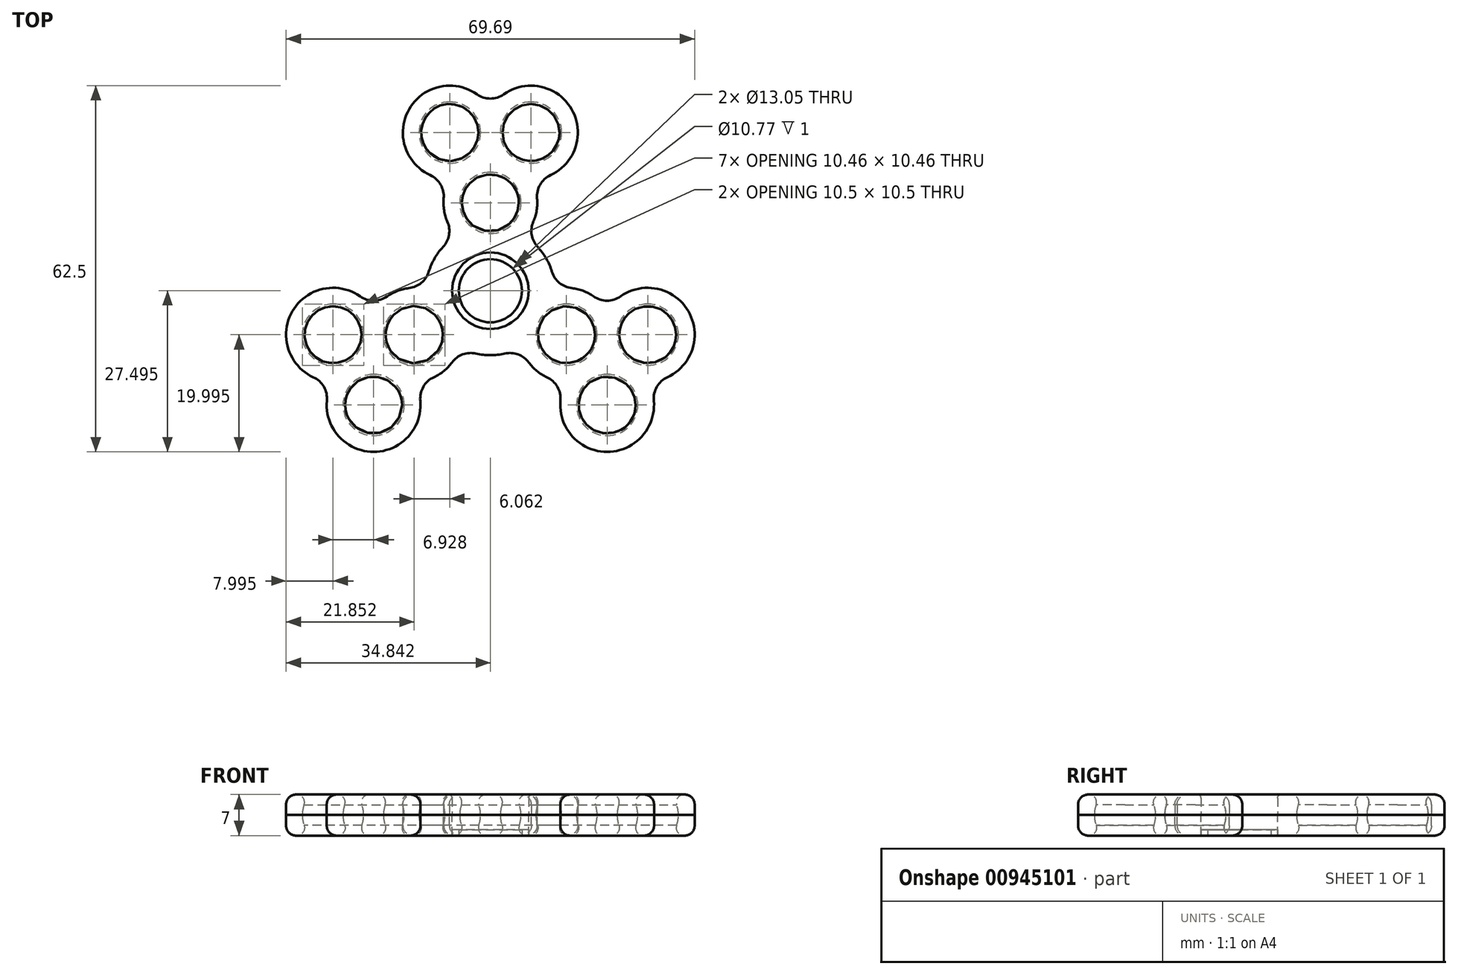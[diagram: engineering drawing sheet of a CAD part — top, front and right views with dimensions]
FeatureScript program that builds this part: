
annotation { "Feature Type Name" : "Feature", "Feature Type Description" : "" }
export const myFeature = defineFeature(function(context is Context, id is Id, definition is map)
    precondition{}
    {
        {
            var Q0;
            Q0=qCreatedBy(makeId("Top.planeOp"),FACE);
            var sketch = newSketch(context, id + "F0", { "sketchPlane" : qUnion([Q0])});
            skCircle(sketch, "E0", {"center": v(73.24, 0.6) * mm, "radius": 6.53 * mm});
            skCircle(sketch, "E1", {"center": v(73.24, 15.6) * mm, "radius": 2.5 * mm});
            skCircle(sketch, "E2", {"center": v(60.25, -6.9) * mm, "radius": 2.5 * mm});
            skCircle(sketch, "E3", {"center": v(86.23, -6.9) * mm, "radius": 2.5 * mm});
            skCircle(sketch, "E4", {"center": v(80.17, 27.6) * mm, "radius": 2.5 * mm});
            skCircle(sketch, "E5", {"center": v(66.31, 27.6) * mm, "radius": 2.5 * mm});
            skCircle(sketch, "E6", {"center": v(46.4, -6.9) * mm, "radius": 2.5 * mm});
            skCircle(sketch, "E7", {"center": v(53.32, -18.9) * mm, "radius": 2.5 * mm});
            skCircle(sketch, "E8", {"center": v(93.16, -18.9) * mm, "radius": 2.5 * mm});
            skCircle(sketch, "E9", {"center": v(100.09, -6.9) * mm, "radius": 2.5 * mm});
            skPoint(sketch, "E10.visualSharp", {"position": v(73.24, 28.6) * mm});
            skPoint(sketch, "E11.visualSharp", {"position": v(68.91, 21.1) * mm});
            skPoint(sketch, "E12.visualSharp", {"position": v(77.57, 21.1) * mm});
            skPoint(sketch, "E13.visualSharp", {"position": v(63.31, -0.6) * mm});
            skPoint(sketch, "E14.visualSharp", {"position": v(67.23, -7.39) * mm});
            skPoint(sketch, "E15.visualSharp", {"position": v(79.25, -7.39) * mm});
            skPoint(sketch, "E16.visualSharp", {"position": v(83.17, -0.6) * mm});
            skPoint(sketch, "E17.visualSharp", {"position": v(77.16, 9.8) * mm});
            skPoint(sketch, "E18.visualSharp", {"position": v(69.32, 9.8) * mm});
            skArc(sketch, "E19.0", {"start": v(59.36, 1.05) * mm, "mid": v(57.4, 0.58) * mm, "end": v(55.63, -0.36) * mm});
            skArc(sketch, "E19.1", {"start": v(65.18, 8.09) * mm, "mid": v(63.72, 6.1) * mm, "end": v(62.73, 3.85) * mm});
            skArc(sketch, "E19.2", {"start": v(65.28, 16.34) * mm, "mid": v(65.34, 14.33) * mm, "end": v(65.9, 12.4) * mm});
            skArc(sketch, "E19.3", {"start": v(70.93, 34.14) * mm, "mid": v(59.39, 31.6) * mm, "end": v(62.97, 20.34) * mm});
            skArc(sketch, "E19.4", {"start": v(79.8, -11.64) * mm, "mid": v(81.18, -13.1) * mm, "end": v(82.88, -14.16) * mm});
            skArc(sketch, "E19.5", {"start": v(70.8, -10.12) * mm, "mid": v(73.24, -10.4) * mm, "end": v(75.69, -10.12) * mm});
            skArc(sketch, "E19.6", {"start": v(63.6, -14.16) * mm, "mid": v(65.3, -13.1) * mm, "end": v(66.69, -11.64) * mm});
            skArc(sketch, "E19.7", {"start": v(45.36, -18.16) * mm, "mid": v(53.32, -26.9) * mm, "end": v(61.29, -18.16) * mm});
            skArc(sketch, "E19.8", {"start": v(85.2, -18.16) * mm, "mid": v(93.16, -26.9) * mm, "end": v(101.13, -18.16) * mm});
            skArc(sketch, "E19.9", {"start": v(103.44, -14.16) * mm, "mid": v(107.02, -2.9) * mm, "end": v(95.47, -0.36) * mm});
            skArc(sketch, "E19.10", {"start": v(90.85, -0.36) * mm, "mid": v(89.08, 0.58) * mm, "end": v(87.13, 1.05) * mm});
            skArc(sketch, "E19.11", {"start": v(83.75, 3.85) * mm, "mid": v(82.77, 6.1) * mm, "end": v(81.3, 8.09) * mm});
            skArc(sketch, "E19.12", {"start": v(51.01, -0.36) * mm, "mid": v(39.47, -2.9) * mm, "end": v(43.05, -14.16) * mm});
            skArc(sketch, "E19.13", {"start": v(80.57, 12.4) * mm, "mid": v(81.14, 14.33) * mm, "end": v(81.2, 16.34) * mm});
            skArc(sketch, "E19.14", {"start": v(83.52, 20.34) * mm, "mid": v(87.1, 31.6) * mm, "end": v(75.55, 34.14) * mm});
            skArc(sketch, "E20.0", {"start": v(45.36, -18.16) * mm, "mid": v(44.84, -15.8) * mm, "end": v(43.05, -14.16) * mm});
            skArc(sketch, "E21.0", {"start": v(63.6, -14.16) * mm, "mid": v(61.8, -15.8) * mm, "end": v(61.29, -18.16) * mm});
            skArc(sketch, "E22.0", {"start": v(70.8, -10.12) * mm, "mid": v(68.52, -10.27) * mm, "end": v(66.69, -11.64) * mm});
            skArc(sketch, "E23.0", {"start": v(79.8, -11.64) * mm, "mid": v(77.97, -10.27) * mm, "end": v(75.69, -10.12) * mm});
            skArc(sketch, "E24.0", {"start": v(85.2, -18.16) * mm, "mid": v(84.68, -15.8) * mm, "end": v(82.88, -14.16) * mm});
            skArc(sketch, "E25.0", {"start": v(103.44, -14.16) * mm, "mid": v(101.65, -15.8) * mm, "end": v(101.13, -18.16) * mm});
            skArc(sketch, "E26.0", {"start": v(90.85, -0.36) * mm, "mid": v(93.16, -1.1) * mm, "end": v(95.47, -0.36) * mm});
            skArc(sketch, "E27.0", {"start": v(83.75, 3.85) * mm, "mid": v(85.02, 1.95) * mm, "end": v(87.13, 1.05) * mm});
            skArc(sketch, "E28.0", {"start": v(80.57, 12.4) * mm, "mid": v(80.3, 10.14) * mm, "end": v(81.3, 8.09) * mm});
            skArc(sketch, "E29.0", {"start": v(83.52, 20.34) * mm, "mid": v(81.73, 18.7) * mm, "end": v(81.2, 16.34) * mm});
            skArc(sketch, "E30.0", {"start": v(65.28, 16.34) * mm, "mid": v(64.76, 18.7) * mm, "end": v(62.97, 20.34) * mm});
            skArc(sketch, "E31.0", {"start": v(65.18, 8.09) * mm, "mid": v(66.19, 10.14) * mm, "end": v(65.9, 12.4) * mm});
            skArc(sketch, "E32.0", {"start": v(59.36, 1.05) * mm, "mid": v(61.46, 1.95) * mm, "end": v(62.73, 3.85) * mm});
            skArc(sketch, "E33.0", {"start": v(51.01, -0.36) * mm, "mid": v(53.32, -1.1) * mm, "end": v(55.63, -0.36) * mm});
            skArc(sketch, "E34.0", {"start": v(70.93, 34.14) * mm, "mid": v(73.24, 33.4) * mm, "end": v(75.55, 34.14) * mm});
            skSolve(sketch);
        }
        {
            var Q0;
            Q0=qSketchRegion(id+"F0",true);
            extrude(context, id + "F1", {"entities" : qUnion([Q0]), "depth" : 3.5 * mm, "offsetDistance" : 25 * mm});
        }
        {
            var Q0;
            Q0=makeQuery(id+"F0.imprint","IMPRINT",FACE,{"disambiguationData":[TD([[makeQuery(id+"F0.imprint","IMPRINT",EDGE,{"derivedFrom":sQuery(id+"F0.wireOp",EDGE,"E0")}),-1.0]])]});
            extrude(context, id + "F2", {"entities" : qUnion([Q0]), "oppositeDirection" : true, "depth" : 3.5 * mm, "offsetDistance" : 25 * mm});
        }
        {
            var Q0;
            Q0=makeQuery(id+"F2.opExtrude","CAP_FACE",FACE,{"disambiguationData":[OSD([sQuery(id+"F0.wireOp",EDGE,"E0"),sQuery(id+"F0.wireOp",EDGE,"tXCEuyxa-6lNA-QPCA-4HXf-ApKYShcEb0Yf"),sQuery(id+"F0.wireOp",EDGE,"E1"),sQuery(id+"F0.wireOp",EDGE,"E2"),sQuery(id+"F0.wireOp",EDGE,"E3"),sQuery(id+"F0.wireOp",EDGE,"E4"),sQuery(id+"F0.wireOp",EDGE,"E5"),sQuery(id+"F0.wireOp",EDGE,"E6"),sQuery(id+"F0.wireOp",EDGE,"E7"),sQuery(id+"F0.wireOp",EDGE,"E8"),sQuery(id+"F0.wireOp",EDGE,"E9"),sQuery(id+"F0.wireOp",EDGE,"0kcF6Lq4-WqBE-dODE-wINV-nyZN5JArXVcS"),sQuery(id+"F0.wireOp",EDGE,"VSrMeVpB-pvXp-ETii-wjF9-Px2PqwZYQnOt"),sQuery(id+"F0.wireOp",EDGE,"OGzEMItw-FQCu-QhKJ-kTiP-AlfaDmg1CYfA"),sQuery(id+"F0.wireOp",EDGE,"E10.filletArc"),sQuery(id+"F0.wireOp",EDGE,"E11.filletArc"),sQuery(id+"F0.wireOp",EDGE,"E12.filletArc"),sQuery(id+"F0.wireOp",EDGE,"61869019-6ff7-477d-8c79-2028de4a396b.trimOffspring"),sQuery(id+"F0.wireOp",EDGE,"b39f1e7b-d492-47c6-a918-6e9c5b166b17"),sQuery(id+"F0.wireOp",EDGE,"9a7d06a7-665d-4e92-ad9d-959fca317462"),sQuery(id+"F0.wireOp",EDGE,"db31c51f-78d2-4091-9bd3-34a254103f45"),sQuery(id+"F0.wireOp",EDGE,"aaf24792-0303-4d5f-86de-c3b2a19fc74e.filletArc"),sQuery(id+"F0.wireOp",EDGE,"5ffe84d5-8cdf-4c2e-9e98-3655a6b86056.filletArc"),sQuery(id+"F0.wireOp",EDGE,"e8945d06-678d-4789-81f5-b1335d2624b7.filletArc"),sQuery(id+"F0.wireOp",EDGE,"a0b45458-2819-4e46-80a9-56e3c7e3f3b4.trimOffspring"),sQuery(id+"F0.wireOp",EDGE,"bf295548-413a-4249-b2ed-de7f7c0a0b82"),sQuery(id+"F0.wireOp",EDGE,"b03dbe81-5cdf-4ba7-a8f7-bb7ec46ab3a8"),sQuery(id+"F0.wireOp",EDGE,"b0d05724-446d-4885-847a-915c569f1139"),sQuery(id+"F0.wireOp",EDGE,"608d76ae-a745-4fd0-ae95-f5732494cd55.filletArc"),sQuery(id+"F0.wireOp",EDGE,"a41367dd-7dbd-4f08-888b-74168a8e5936.filletArc"),sQuery(id+"F0.wireOp",EDGE,"84e31002-7089-4eef-81a0-79c8965d61ed.filletArc"),sQuery(id+"F0.wireOp",EDGE,"1335fa2d-2410-4889-a90b-ae026db059b2.trimOffspring"),sQuery(id+"F0.wireOp",EDGE,"81157b49-ae94-446f-8b4e-5ce1e116e724.trimOffspring"),sQuery(id+"F0.wireOp",EDGE,"4f1c551e-3bfd-48a9-873a-6291d27f8455.trimOffspring"),sQuery(id+"F0.wireOp",EDGE,"E13.filletArc"),sQuery(id+"F0.wireOp",EDGE,"E14.filletArc"),sQuery(id+"F0.wireOp",EDGE,"E15.filletArc"),sQuery(id+"F0.wireOp",EDGE,"E16.filletArc"),sQuery(id+"F0.wireOp",EDGE,"E17.filletArc"),sQuery(id+"F0.wireOp",EDGE,"E18.filletArc")])],"isStart":true});
            var sketch = newSketch(context, id + "F3", { "sketchPlane" : qUnion([Q0])});
            skLineSegment(sketch, "E35", {"start": v(53.32, -18.9) * mm, "end": v(53.32, -24.12) * mm});
            skLineSegment(sketch, "E36", {"start": v(53.32, -18.9) * mm, "end": v(53.32, -13.66) * mm});
            skArc(sketch, "E37", {"start": v(53.32, -13.66) * mm, "mid": v(48.1, -18.9) * mm, "end": v(53.32, -24.12) * mm});
            skSolve(sketch);
        }
        {
            var Q0;
            Q0=qSketchRegion(id+"F3",true);
            var Q1;
            Q1=sQuery(id+"F3.wireOp",EDGE,"E36");
            revolve(context, id + "F4", {"surfaceOperationType" : NewSurfaceOperationType.NEW, "entities" : qUnion([Q0]), "axis" : qUnion([Q1]), "revolveType" : RevolveType.FULL});
        }
        {
            var Q0;
            Q0=makeQuery(id+"F2.opExtrude","CAP_FACE",FACE,{"disambiguationData":[OSD([sQuery(id+"F0.wireOp",EDGE,"E0"),sQuery(id+"F0.wireOp",EDGE,"tXCEuyxa-6lNA-QPCA-4HXf-ApKYShcEb0Yf"),sQuery(id+"F0.wireOp",EDGE,"E1"),sQuery(id+"F0.wireOp",EDGE,"E2"),sQuery(id+"F0.wireOp",EDGE,"E3"),sQuery(id+"F0.wireOp",EDGE,"E4"),sQuery(id+"F0.wireOp",EDGE,"E5"),sQuery(id+"F0.wireOp",EDGE,"E6"),sQuery(id+"F0.wireOp",EDGE,"E7"),sQuery(id+"F0.wireOp",EDGE,"E8"),sQuery(id+"F0.wireOp",EDGE,"E9"),sQuery(id+"F0.wireOp",EDGE,"0kcF6Lq4-WqBE-dODE-wINV-nyZN5JArXVcS"),sQuery(id+"F0.wireOp",EDGE,"VSrMeVpB-pvXp-ETii-wjF9-Px2PqwZYQnOt"),sQuery(id+"F0.wireOp",EDGE,"OGzEMItw-FQCu-QhKJ-kTiP-AlfaDmg1CYfA"),sQuery(id+"F0.wireOp",EDGE,"E10.filletArc"),sQuery(id+"F0.wireOp",EDGE,"E11.filletArc"),sQuery(id+"F0.wireOp",EDGE,"E12.filletArc"),sQuery(id+"F0.wireOp",EDGE,"61869019-6ff7-477d-8c79-2028de4a396b.trimOffspring"),sQuery(id+"F0.wireOp",EDGE,"b39f1e7b-d492-47c6-a918-6e9c5b166b17"),sQuery(id+"F0.wireOp",EDGE,"9a7d06a7-665d-4e92-ad9d-959fca317462"),sQuery(id+"F0.wireOp",EDGE,"db31c51f-78d2-4091-9bd3-34a254103f45"),sQuery(id+"F0.wireOp",EDGE,"aaf24792-0303-4d5f-86de-c3b2a19fc74e.filletArc"),sQuery(id+"F0.wireOp",EDGE,"5ffe84d5-8cdf-4c2e-9e98-3655a6b86056.filletArc"),sQuery(id+"F0.wireOp",EDGE,"e8945d06-678d-4789-81f5-b1335d2624b7.filletArc"),sQuery(id+"F0.wireOp",EDGE,"a0b45458-2819-4e46-80a9-56e3c7e3f3b4.trimOffspring"),sQuery(id+"F0.wireOp",EDGE,"bf295548-413a-4249-b2ed-de7f7c0a0b82"),sQuery(id+"F0.wireOp",EDGE,"b03dbe81-5cdf-4ba7-a8f7-bb7ec46ab3a8"),sQuery(id+"F0.wireOp",EDGE,"b0d05724-446d-4885-847a-915c569f1139"),sQuery(id+"F0.wireOp",EDGE,"608d76ae-a745-4fd0-ae95-f5732494cd55.filletArc"),sQuery(id+"F0.wireOp",EDGE,"a41367dd-7dbd-4f08-888b-74168a8e5936.filletArc"),sQuery(id+"F0.wireOp",EDGE,"84e31002-7089-4eef-81a0-79c8965d61ed.filletArc"),sQuery(id+"F0.wireOp",EDGE,"1335fa2d-2410-4889-a90b-ae026db059b2.trimOffspring"),sQuery(id+"F0.wireOp",EDGE,"81157b49-ae94-446f-8b4e-5ce1e116e724.trimOffspring"),sQuery(id+"F0.wireOp",EDGE,"4f1c551e-3bfd-48a9-873a-6291d27f8455.trimOffspring"),sQuery(id+"F0.wireOp",EDGE,"E13.filletArc"),sQuery(id+"F0.wireOp",EDGE,"E14.filletArc"),sQuery(id+"F0.wireOp",EDGE,"E15.filletArc"),sQuery(id+"F0.wireOp",EDGE,"E16.filletArc"),sQuery(id+"F0.wireOp",EDGE,"E17.filletArc"),sQuery(id+"F0.wireOp",EDGE,"E18.filletArc")])],"isStart":true});
            var sketch = newSketch(context, id + "F5", { "sketchPlane" : qUnion([Q0])});
            skLineSegment(sketch, "E38", {"start": v(60.25, -6.9) * mm, "end": v(60.25, -12.14) * mm});
            skLineSegment(sketch, "E39", {"start": v(60.25, -6.9) * mm, "end": v(60.25, -1.64) * mm});
            skArc(sketch, "E40", {"start": v(60.25, -1.64) * mm, "mid": v(55, -6.9) * mm, "end": v(60.25, -12.14) * mm});
            skSolve(sketch);
        }
        {
            var Q0;
            Q0=makeQuery(id+"F2.opExtrude","CAP_FACE",FACE,{"disambiguationData":[OSD([sQuery(id+"F0.wireOp",EDGE,"E0"),sQuery(id+"F0.wireOp",EDGE,"tXCEuyxa-6lNA-QPCA-4HXf-ApKYShcEb0Yf"),sQuery(id+"F0.wireOp",EDGE,"E1"),sQuery(id+"F0.wireOp",EDGE,"E2"),sQuery(id+"F0.wireOp",EDGE,"E3"),sQuery(id+"F0.wireOp",EDGE,"E4"),sQuery(id+"F0.wireOp",EDGE,"E5"),sQuery(id+"F0.wireOp",EDGE,"E6"),sQuery(id+"F0.wireOp",EDGE,"E7"),sQuery(id+"F0.wireOp",EDGE,"E8"),sQuery(id+"F0.wireOp",EDGE,"E9"),sQuery(id+"F0.wireOp",EDGE,"0kcF6Lq4-WqBE-dODE-wINV-nyZN5JArXVcS"),sQuery(id+"F0.wireOp",EDGE,"VSrMeVpB-pvXp-ETii-wjF9-Px2PqwZYQnOt"),sQuery(id+"F0.wireOp",EDGE,"OGzEMItw-FQCu-QhKJ-kTiP-AlfaDmg1CYfA"),sQuery(id+"F0.wireOp",EDGE,"E10.filletArc"),sQuery(id+"F0.wireOp",EDGE,"E11.filletArc"),sQuery(id+"F0.wireOp",EDGE,"E12.filletArc"),sQuery(id+"F0.wireOp",EDGE,"61869019-6ff7-477d-8c79-2028de4a396b.trimOffspring"),sQuery(id+"F0.wireOp",EDGE,"b39f1e7b-d492-47c6-a918-6e9c5b166b17"),sQuery(id+"F0.wireOp",EDGE,"9a7d06a7-665d-4e92-ad9d-959fca317462"),sQuery(id+"F0.wireOp",EDGE,"db31c51f-78d2-4091-9bd3-34a254103f45"),sQuery(id+"F0.wireOp",EDGE,"aaf24792-0303-4d5f-86de-c3b2a19fc74e.filletArc"),sQuery(id+"F0.wireOp",EDGE,"5ffe84d5-8cdf-4c2e-9e98-3655a6b86056.filletArc"),sQuery(id+"F0.wireOp",EDGE,"e8945d06-678d-4789-81f5-b1335d2624b7.filletArc"),sQuery(id+"F0.wireOp",EDGE,"a0b45458-2819-4e46-80a9-56e3c7e3f3b4.trimOffspring"),sQuery(id+"F0.wireOp",EDGE,"bf295548-413a-4249-b2ed-de7f7c0a0b82"),sQuery(id+"F0.wireOp",EDGE,"b03dbe81-5cdf-4ba7-a8f7-bb7ec46ab3a8"),sQuery(id+"F0.wireOp",EDGE,"b0d05724-446d-4885-847a-915c569f1139"),sQuery(id+"F0.wireOp",EDGE,"608d76ae-a745-4fd0-ae95-f5732494cd55.filletArc"),sQuery(id+"F0.wireOp",EDGE,"a41367dd-7dbd-4f08-888b-74168a8e5936.filletArc"),sQuery(id+"F0.wireOp",EDGE,"84e31002-7089-4eef-81a0-79c8965d61ed.filletArc"),sQuery(id+"F0.wireOp",EDGE,"1335fa2d-2410-4889-a90b-ae026db059b2.trimOffspring"),sQuery(id+"F0.wireOp",EDGE,"81157b49-ae94-446f-8b4e-5ce1e116e724.trimOffspring"),sQuery(id+"F0.wireOp",EDGE,"4f1c551e-3bfd-48a9-873a-6291d27f8455.trimOffspring"),sQuery(id+"F0.wireOp",EDGE,"E13.filletArc"),sQuery(id+"F0.wireOp",EDGE,"E14.filletArc"),sQuery(id+"F0.wireOp",EDGE,"E15.filletArc"),sQuery(id+"F0.wireOp",EDGE,"E16.filletArc"),sQuery(id+"F0.wireOp",EDGE,"E17.filletArc"),sQuery(id+"F0.wireOp",EDGE,"E18.filletArc")])],"isStart":true});
            var sketch = newSketch(context, id + "F6", { "sketchPlane" : qUnion([Q0])});
            skLineSegment(sketch, "E41", {"start": v(93.16, -18.9) * mm, "end": v(93.16, -24.12) * mm});
            skArc(sketch, "E42", {"start": v(93.16, -13.66) * mm, "mid": v(87.93, -18.9) * mm, "end": v(93.16, -24.12) * mm});
            skLineSegment(sketch, "E43", {"start": v(93.16, -18.9) * mm, "end": v(93.16, -13.66) * mm});
            skSolve(sketch);
        }
        {
            var Q0;
            Q0=qSketchRegion(id+"F6",true);
            var Q1;
            Q1=sQuery(id+"F6.wireOp",EDGE,"E43");
            revolve(context, id + "F7", {"surfaceOperationType" : NewSurfaceOperationType.NEW, "entities" : qUnion([Q0]), "axis" : qUnion([Q1]), "revolveType" : RevolveType.FULL});
        }
        {
            var Q0;
            Q0=makeQuery(id+"F2.opExtrude","CAP_FACE",FACE,{"disambiguationData":[OSD([sQuery(id+"F0.wireOp",EDGE,"E0"),sQuery(id+"F0.wireOp",EDGE,"tXCEuyxa-6lNA-QPCA-4HXf-ApKYShcEb0Yf"),sQuery(id+"F0.wireOp",EDGE,"E1"),sQuery(id+"F0.wireOp",EDGE,"E2"),sQuery(id+"F0.wireOp",EDGE,"E3"),sQuery(id+"F0.wireOp",EDGE,"E4"),sQuery(id+"F0.wireOp",EDGE,"E5"),sQuery(id+"F0.wireOp",EDGE,"E6"),sQuery(id+"F0.wireOp",EDGE,"E7"),sQuery(id+"F0.wireOp",EDGE,"E8"),sQuery(id+"F0.wireOp",EDGE,"E9"),sQuery(id+"F0.wireOp",EDGE,"0kcF6Lq4-WqBE-dODE-wINV-nyZN5JArXVcS"),sQuery(id+"F0.wireOp",EDGE,"VSrMeVpB-pvXp-ETii-wjF9-Px2PqwZYQnOt"),sQuery(id+"F0.wireOp",EDGE,"OGzEMItw-FQCu-QhKJ-kTiP-AlfaDmg1CYfA"),sQuery(id+"F0.wireOp",EDGE,"E10.filletArc"),sQuery(id+"F0.wireOp",EDGE,"E11.filletArc"),sQuery(id+"F0.wireOp",EDGE,"E12.filletArc"),sQuery(id+"F0.wireOp",EDGE,"61869019-6ff7-477d-8c79-2028de4a396b.trimOffspring"),sQuery(id+"F0.wireOp",EDGE,"b39f1e7b-d492-47c6-a918-6e9c5b166b17"),sQuery(id+"F0.wireOp",EDGE,"9a7d06a7-665d-4e92-ad9d-959fca317462"),sQuery(id+"F0.wireOp",EDGE,"db31c51f-78d2-4091-9bd3-34a254103f45"),sQuery(id+"F0.wireOp",EDGE,"aaf24792-0303-4d5f-86de-c3b2a19fc74e.filletArc"),sQuery(id+"F0.wireOp",EDGE,"5ffe84d5-8cdf-4c2e-9e98-3655a6b86056.filletArc"),sQuery(id+"F0.wireOp",EDGE,"e8945d06-678d-4789-81f5-b1335d2624b7.filletArc"),sQuery(id+"F0.wireOp",EDGE,"a0b45458-2819-4e46-80a9-56e3c7e3f3b4.trimOffspring"),sQuery(id+"F0.wireOp",EDGE,"bf295548-413a-4249-b2ed-de7f7c0a0b82"),sQuery(id+"F0.wireOp",EDGE,"b03dbe81-5cdf-4ba7-a8f7-bb7ec46ab3a8"),sQuery(id+"F0.wireOp",EDGE,"b0d05724-446d-4885-847a-915c569f1139"),sQuery(id+"F0.wireOp",EDGE,"608d76ae-a745-4fd0-ae95-f5732494cd55.filletArc"),sQuery(id+"F0.wireOp",EDGE,"a41367dd-7dbd-4f08-888b-74168a8e5936.filletArc"),sQuery(id+"F0.wireOp",EDGE,"84e31002-7089-4eef-81a0-79c8965d61ed.filletArc"),sQuery(id+"F0.wireOp",EDGE,"1335fa2d-2410-4889-a90b-ae026db059b2.trimOffspring"),sQuery(id+"F0.wireOp",EDGE,"81157b49-ae94-446f-8b4e-5ce1e116e724.trimOffspring"),sQuery(id+"F0.wireOp",EDGE,"4f1c551e-3bfd-48a9-873a-6291d27f8455.trimOffspring"),sQuery(id+"F0.wireOp",EDGE,"E13.filletArc"),sQuery(id+"F0.wireOp",EDGE,"E14.filletArc"),sQuery(id+"F0.wireOp",EDGE,"E15.filletArc"),sQuery(id+"F0.wireOp",EDGE,"E16.filletArc"),sQuery(id+"F0.wireOp",EDGE,"E17.filletArc"),sQuery(id+"F0.wireOp",EDGE,"E18.filletArc")])],"isStart":true});
            var sketch = newSketch(context, id + "F8", { "sketchPlane" : qUnion([Q0])});
            skLineSegment(sketch, "E44", {"start": v(86.23, -6.9) * mm, "end": v(86.23, -12.12) * mm});
            skArc(sketch, "E45", {"start": v(86.23, -1.66) * mm, "mid": v(81, -6.9) * mm, "end": v(86.23, -12.12) * mm});
            skLineSegment(sketch, "E46", {"start": v(86.23, -6.9) * mm, "end": v(86.23, -1.66) * mm});
            skSolve(sketch);
        }
        {
            var Q0;
            Q0=qSketchRegion(id+"F8",true);
            var Q1;
            Q1=sQuery(id+"F8.wireOp",EDGE,"E46");
            revolve(context, id + "F9", {"surfaceOperationType" : NewSurfaceOperationType.NEW, "entities" : qUnion([Q0]), "axis" : qUnion([Q1]), "revolveType" : RevolveType.FULL});
        }
        {
            var Q0;
            Q0=makeQuery(id+"F2.opExtrude","CAP_FACE",FACE,{"disambiguationData":[OSD([sQuery(id+"F0.wireOp",EDGE,"E0"),sQuery(id+"F0.wireOp",EDGE,"tXCEuyxa-6lNA-QPCA-4HXf-ApKYShcEb0Yf"),sQuery(id+"F0.wireOp",EDGE,"E1"),sQuery(id+"F0.wireOp",EDGE,"E2"),sQuery(id+"F0.wireOp",EDGE,"E3"),sQuery(id+"F0.wireOp",EDGE,"E4"),sQuery(id+"F0.wireOp",EDGE,"E5"),sQuery(id+"F0.wireOp",EDGE,"E6"),sQuery(id+"F0.wireOp",EDGE,"E7"),sQuery(id+"F0.wireOp",EDGE,"E8"),sQuery(id+"F0.wireOp",EDGE,"E9"),sQuery(id+"F0.wireOp",EDGE,"0kcF6Lq4-WqBE-dODE-wINV-nyZN5JArXVcS"),sQuery(id+"F0.wireOp",EDGE,"VSrMeVpB-pvXp-ETii-wjF9-Px2PqwZYQnOt"),sQuery(id+"F0.wireOp",EDGE,"OGzEMItw-FQCu-QhKJ-kTiP-AlfaDmg1CYfA"),sQuery(id+"F0.wireOp",EDGE,"E10.filletArc"),sQuery(id+"F0.wireOp",EDGE,"E11.filletArc"),sQuery(id+"F0.wireOp",EDGE,"E12.filletArc"),sQuery(id+"F0.wireOp",EDGE,"61869019-6ff7-477d-8c79-2028de4a396b.trimOffspring"),sQuery(id+"F0.wireOp",EDGE,"b39f1e7b-d492-47c6-a918-6e9c5b166b17"),sQuery(id+"F0.wireOp",EDGE,"9a7d06a7-665d-4e92-ad9d-959fca317462"),sQuery(id+"F0.wireOp",EDGE,"db31c51f-78d2-4091-9bd3-34a254103f45"),sQuery(id+"F0.wireOp",EDGE,"aaf24792-0303-4d5f-86de-c3b2a19fc74e.filletArc"),sQuery(id+"F0.wireOp",EDGE,"5ffe84d5-8cdf-4c2e-9e98-3655a6b86056.filletArc"),sQuery(id+"F0.wireOp",EDGE,"e8945d06-678d-4789-81f5-b1335d2624b7.filletArc"),sQuery(id+"F0.wireOp",EDGE,"a0b45458-2819-4e46-80a9-56e3c7e3f3b4.trimOffspring"),sQuery(id+"F0.wireOp",EDGE,"bf295548-413a-4249-b2ed-de7f7c0a0b82"),sQuery(id+"F0.wireOp",EDGE,"b03dbe81-5cdf-4ba7-a8f7-bb7ec46ab3a8"),sQuery(id+"F0.wireOp",EDGE,"b0d05724-446d-4885-847a-915c569f1139"),sQuery(id+"F0.wireOp",EDGE,"608d76ae-a745-4fd0-ae95-f5732494cd55.filletArc"),sQuery(id+"F0.wireOp",EDGE,"a41367dd-7dbd-4f08-888b-74168a8e5936.filletArc"),sQuery(id+"F0.wireOp",EDGE,"84e31002-7089-4eef-81a0-79c8965d61ed.filletArc"),sQuery(id+"F0.wireOp",EDGE,"1335fa2d-2410-4889-a90b-ae026db059b2.trimOffspring"),sQuery(id+"F0.wireOp",EDGE,"81157b49-ae94-446f-8b4e-5ce1e116e724.trimOffspring"),sQuery(id+"F0.wireOp",EDGE,"4f1c551e-3bfd-48a9-873a-6291d27f8455.trimOffspring"),sQuery(id+"F0.wireOp",EDGE,"E13.filletArc"),sQuery(id+"F0.wireOp",EDGE,"E14.filletArc"),sQuery(id+"F0.wireOp",EDGE,"E15.filletArc"),sQuery(id+"F0.wireOp",EDGE,"E16.filletArc"),sQuery(id+"F0.wireOp",EDGE,"E17.filletArc"),sQuery(id+"F0.wireOp",EDGE,"E18.filletArc")])],"isStart":true});
            var sketch = newSketch(context, id + "F10", { "sketchPlane" : qUnion([Q0])});
            skLineSegment(sketch, "E47", {"start": v(100.09, -6.9) * mm, "end": v(100.09, -12.12) * mm});
            skArc(sketch, "E48", {"start": v(100.09, -1.66) * mm, "mid": v(94.86, -6.9) * mm, "end": v(100.09, -12.12) * mm});
            skLineSegment(sketch, "E49", {"start": v(100.09, -6.9) * mm, "end": v(100.09, -1.66) * mm});
            skSolve(sketch);
        }
        {
            var Q0;
            Q0=qSketchRegion(id+"F10",true);
            var Q1;
            Q1=sQuery(id+"F10.wireOp",EDGE,"E47");
            revolve(context, id + "F11", {"surfaceOperationType" : NewSurfaceOperationType.NEW, "entities" : qUnion([Q0]), "axis" : qUnion([Q1]), "revolveType" : RevolveType.FULL});
        }
        {
            var Q0;
            Q0=makeQuery(id+"F2.opExtrude","CAP_FACE",FACE,{"disambiguationData":[OSD([sQuery(id+"F0.wireOp",EDGE,"E0"),sQuery(id+"F0.wireOp",EDGE,"tXCEuyxa-6lNA-QPCA-4HXf-ApKYShcEb0Yf"),sQuery(id+"F0.wireOp",EDGE,"E1"),sQuery(id+"F0.wireOp",EDGE,"E2"),sQuery(id+"F0.wireOp",EDGE,"E3"),sQuery(id+"F0.wireOp",EDGE,"E4"),sQuery(id+"F0.wireOp",EDGE,"E5"),sQuery(id+"F0.wireOp",EDGE,"E6"),sQuery(id+"F0.wireOp",EDGE,"E7"),sQuery(id+"F0.wireOp",EDGE,"E8"),sQuery(id+"F0.wireOp",EDGE,"E9"),sQuery(id+"F0.wireOp",EDGE,"0kcF6Lq4-WqBE-dODE-wINV-nyZN5JArXVcS"),sQuery(id+"F0.wireOp",EDGE,"VSrMeVpB-pvXp-ETii-wjF9-Px2PqwZYQnOt"),sQuery(id+"F0.wireOp",EDGE,"OGzEMItw-FQCu-QhKJ-kTiP-AlfaDmg1CYfA"),sQuery(id+"F0.wireOp",EDGE,"E10.filletArc"),sQuery(id+"F0.wireOp",EDGE,"E11.filletArc"),sQuery(id+"F0.wireOp",EDGE,"E12.filletArc"),sQuery(id+"F0.wireOp",EDGE,"61869019-6ff7-477d-8c79-2028de4a396b.trimOffspring"),sQuery(id+"F0.wireOp",EDGE,"b39f1e7b-d492-47c6-a918-6e9c5b166b17"),sQuery(id+"F0.wireOp",EDGE,"9a7d06a7-665d-4e92-ad9d-959fca317462"),sQuery(id+"F0.wireOp",EDGE,"db31c51f-78d2-4091-9bd3-34a254103f45"),sQuery(id+"F0.wireOp",EDGE,"aaf24792-0303-4d5f-86de-c3b2a19fc74e.filletArc"),sQuery(id+"F0.wireOp",EDGE,"5ffe84d5-8cdf-4c2e-9e98-3655a6b86056.filletArc"),sQuery(id+"F0.wireOp",EDGE,"e8945d06-678d-4789-81f5-b1335d2624b7.filletArc"),sQuery(id+"F0.wireOp",EDGE,"a0b45458-2819-4e46-80a9-56e3c7e3f3b4.trimOffspring"),sQuery(id+"F0.wireOp",EDGE,"bf295548-413a-4249-b2ed-de7f7c0a0b82"),sQuery(id+"F0.wireOp",EDGE,"b03dbe81-5cdf-4ba7-a8f7-bb7ec46ab3a8"),sQuery(id+"F0.wireOp",EDGE,"b0d05724-446d-4885-847a-915c569f1139"),sQuery(id+"F0.wireOp",EDGE,"608d76ae-a745-4fd0-ae95-f5732494cd55.filletArc"),sQuery(id+"F0.wireOp",EDGE,"a41367dd-7dbd-4f08-888b-74168a8e5936.filletArc"),sQuery(id+"F0.wireOp",EDGE,"84e31002-7089-4eef-81a0-79c8965d61ed.filletArc"),sQuery(id+"F0.wireOp",EDGE,"1335fa2d-2410-4889-a90b-ae026db059b2.trimOffspring"),sQuery(id+"F0.wireOp",EDGE,"81157b49-ae94-446f-8b4e-5ce1e116e724.trimOffspring"),sQuery(id+"F0.wireOp",EDGE,"4f1c551e-3bfd-48a9-873a-6291d27f8455.trimOffspring"),sQuery(id+"F0.wireOp",EDGE,"E13.filletArc"),sQuery(id+"F0.wireOp",EDGE,"E14.filletArc"),sQuery(id+"F0.wireOp",EDGE,"E15.filletArc"),sQuery(id+"F0.wireOp",EDGE,"E16.filletArc"),sQuery(id+"F0.wireOp",EDGE,"E17.filletArc"),sQuery(id+"F0.wireOp",EDGE,"E18.filletArc")])],"isStart":true});
            var sketch = newSketch(context, id + "F12", { "sketchPlane" : qUnion([Q0])});
            skLineSegment(sketch, "E50", {"start": v(73.24, 15.6) * mm, "end": v(73.24, 10.38) * mm});
            skArc(sketch, "E51", {"start": v(73.24, 20.84) * mm, "mid": v(68.01, 15.6) * mm, "end": v(73.24, 10.38) * mm});
            skLineSegment(sketch, "E52", {"start": v(73.24, 15.6) * mm, "end": v(73.24, 20.84) * mm});
            skSolve(sketch);
        }
        {
            var Q0;
            Q0=qSketchRegion(id+"F12",true);
            var Q1;
            Q1=sQuery(id+"F12.wireOp",EDGE,"E50");
            revolve(context, id + "F13", {"surfaceOperationType" : NewSurfaceOperationType.NEW, "entities" : qUnion([Q0]), "axis" : qUnion([Q1]), "revolveType" : RevolveType.FULL});
        }
        {
            var Q0;
            Q0=makeQuery(id+"F2.opExtrude","CAP_FACE",FACE,{"disambiguationData":[OSD([sQuery(id+"F0.wireOp",EDGE,"E0"),sQuery(id+"F0.wireOp",EDGE,"tXCEuyxa-6lNA-QPCA-4HXf-ApKYShcEb0Yf"),sQuery(id+"F0.wireOp",EDGE,"E1"),sQuery(id+"F0.wireOp",EDGE,"E2"),sQuery(id+"F0.wireOp",EDGE,"E3"),sQuery(id+"F0.wireOp",EDGE,"E4"),sQuery(id+"F0.wireOp",EDGE,"E5"),sQuery(id+"F0.wireOp",EDGE,"E6"),sQuery(id+"F0.wireOp",EDGE,"E7"),sQuery(id+"F0.wireOp",EDGE,"E8"),sQuery(id+"F0.wireOp",EDGE,"E9"),sQuery(id+"F0.wireOp",EDGE,"0kcF6Lq4-WqBE-dODE-wINV-nyZN5JArXVcS"),sQuery(id+"F0.wireOp",EDGE,"VSrMeVpB-pvXp-ETii-wjF9-Px2PqwZYQnOt"),sQuery(id+"F0.wireOp",EDGE,"OGzEMItw-FQCu-QhKJ-kTiP-AlfaDmg1CYfA"),sQuery(id+"F0.wireOp",EDGE,"E10.filletArc"),sQuery(id+"F0.wireOp",EDGE,"E11.filletArc"),sQuery(id+"F0.wireOp",EDGE,"E12.filletArc"),sQuery(id+"F0.wireOp",EDGE,"61869019-6ff7-477d-8c79-2028de4a396b.trimOffspring"),sQuery(id+"F0.wireOp",EDGE,"b39f1e7b-d492-47c6-a918-6e9c5b166b17"),sQuery(id+"F0.wireOp",EDGE,"9a7d06a7-665d-4e92-ad9d-959fca317462"),sQuery(id+"F0.wireOp",EDGE,"db31c51f-78d2-4091-9bd3-34a254103f45"),sQuery(id+"F0.wireOp",EDGE,"aaf24792-0303-4d5f-86de-c3b2a19fc74e.filletArc"),sQuery(id+"F0.wireOp",EDGE,"5ffe84d5-8cdf-4c2e-9e98-3655a6b86056.filletArc"),sQuery(id+"F0.wireOp",EDGE,"e8945d06-678d-4789-81f5-b1335d2624b7.filletArc"),sQuery(id+"F0.wireOp",EDGE,"a0b45458-2819-4e46-80a9-56e3c7e3f3b4.trimOffspring"),sQuery(id+"F0.wireOp",EDGE,"bf295548-413a-4249-b2ed-de7f7c0a0b82"),sQuery(id+"F0.wireOp",EDGE,"b03dbe81-5cdf-4ba7-a8f7-bb7ec46ab3a8"),sQuery(id+"F0.wireOp",EDGE,"b0d05724-446d-4885-847a-915c569f1139"),sQuery(id+"F0.wireOp",EDGE,"608d76ae-a745-4fd0-ae95-f5732494cd55.filletArc"),sQuery(id+"F0.wireOp",EDGE,"a41367dd-7dbd-4f08-888b-74168a8e5936.filletArc"),sQuery(id+"F0.wireOp",EDGE,"84e31002-7089-4eef-81a0-79c8965d61ed.filletArc"),sQuery(id+"F0.wireOp",EDGE,"1335fa2d-2410-4889-a90b-ae026db059b2.trimOffspring"),sQuery(id+"F0.wireOp",EDGE,"81157b49-ae94-446f-8b4e-5ce1e116e724.trimOffspring"),sQuery(id+"F0.wireOp",EDGE,"4f1c551e-3bfd-48a9-873a-6291d27f8455.trimOffspring"),sQuery(id+"F0.wireOp",EDGE,"E13.filletArc"),sQuery(id+"F0.wireOp",EDGE,"E14.filletArc"),sQuery(id+"F0.wireOp",EDGE,"E15.filletArc"),sQuery(id+"F0.wireOp",EDGE,"E16.filletArc"),sQuery(id+"F0.wireOp",EDGE,"E17.filletArc"),sQuery(id+"F0.wireOp",EDGE,"E18.filletArc")])],"isStart":true});
            var sketch = newSketch(context, id + "F14", { "sketchPlane" : qUnion([Q0])});
            skLineSegment(sketch, "E53", {"start": v(66.31, 27.6) * mm, "end": v(66.31, 22.36) * mm});
            skArc(sketch, "E54", {"start": v(66.31, 32.86) * mm, "mid": v(61.06, 27.6) * mm, "end": v(66.31, 22.36) * mm});
            skLineSegment(sketch, "E55", {"start": v(66.31, 27.6) * mm, "end": v(66.31, 32.86) * mm});
            skSolve(sketch);
        }
        {
            var Q0;
            Q0=qSketchRegion(id+"F14",true);
            var Q1;
            Q1=sQuery(id+"F14.wireOp",EDGE,"E53");
            revolve(context, id + "F15", {"surfaceOperationType" : NewSurfaceOperationType.NEW, "entities" : qUnion([Q0]), "axis" : qUnion([Q1]), "revolveType" : RevolveType.FULL});
        }
        {
            var Q0;
            Q0=makeQuery(id+"F2.opExtrude","CAP_FACE",FACE,{"disambiguationData":[OSD([sQuery(id+"F0.wireOp",EDGE,"E0"),sQuery(id+"F0.wireOp",EDGE,"tXCEuyxa-6lNA-QPCA-4HXf-ApKYShcEb0Yf"),sQuery(id+"F0.wireOp",EDGE,"E1"),sQuery(id+"F0.wireOp",EDGE,"E2"),sQuery(id+"F0.wireOp",EDGE,"E3"),sQuery(id+"F0.wireOp",EDGE,"E4"),sQuery(id+"F0.wireOp",EDGE,"E5"),sQuery(id+"F0.wireOp",EDGE,"E6"),sQuery(id+"F0.wireOp",EDGE,"E7"),sQuery(id+"F0.wireOp",EDGE,"E8"),sQuery(id+"F0.wireOp",EDGE,"E9"),sQuery(id+"F0.wireOp",EDGE,"0kcF6Lq4-WqBE-dODE-wINV-nyZN5JArXVcS"),sQuery(id+"F0.wireOp",EDGE,"VSrMeVpB-pvXp-ETii-wjF9-Px2PqwZYQnOt"),sQuery(id+"F0.wireOp",EDGE,"OGzEMItw-FQCu-QhKJ-kTiP-AlfaDmg1CYfA"),sQuery(id+"F0.wireOp",EDGE,"E10.filletArc"),sQuery(id+"F0.wireOp",EDGE,"E11.filletArc"),sQuery(id+"F0.wireOp",EDGE,"E12.filletArc"),sQuery(id+"F0.wireOp",EDGE,"61869019-6ff7-477d-8c79-2028de4a396b.trimOffspring"),sQuery(id+"F0.wireOp",EDGE,"b39f1e7b-d492-47c6-a918-6e9c5b166b17"),sQuery(id+"F0.wireOp",EDGE,"9a7d06a7-665d-4e92-ad9d-959fca317462"),sQuery(id+"F0.wireOp",EDGE,"db31c51f-78d2-4091-9bd3-34a254103f45"),sQuery(id+"F0.wireOp",EDGE,"aaf24792-0303-4d5f-86de-c3b2a19fc74e.filletArc"),sQuery(id+"F0.wireOp",EDGE,"5ffe84d5-8cdf-4c2e-9e98-3655a6b86056.filletArc"),sQuery(id+"F0.wireOp",EDGE,"e8945d06-678d-4789-81f5-b1335d2624b7.filletArc"),sQuery(id+"F0.wireOp",EDGE,"a0b45458-2819-4e46-80a9-56e3c7e3f3b4.trimOffspring"),sQuery(id+"F0.wireOp",EDGE,"bf295548-413a-4249-b2ed-de7f7c0a0b82"),sQuery(id+"F0.wireOp",EDGE,"b03dbe81-5cdf-4ba7-a8f7-bb7ec46ab3a8"),sQuery(id+"F0.wireOp",EDGE,"b0d05724-446d-4885-847a-915c569f1139"),sQuery(id+"F0.wireOp",EDGE,"608d76ae-a745-4fd0-ae95-f5732494cd55.filletArc"),sQuery(id+"F0.wireOp",EDGE,"a41367dd-7dbd-4f08-888b-74168a8e5936.filletArc"),sQuery(id+"F0.wireOp",EDGE,"84e31002-7089-4eef-81a0-79c8965d61ed.filletArc"),sQuery(id+"F0.wireOp",EDGE,"1335fa2d-2410-4889-a90b-ae026db059b2.trimOffspring"),sQuery(id+"F0.wireOp",EDGE,"81157b49-ae94-446f-8b4e-5ce1e116e724.trimOffspring"),sQuery(id+"F0.wireOp",EDGE,"4f1c551e-3bfd-48a9-873a-6291d27f8455.trimOffspring"),sQuery(id+"F0.wireOp",EDGE,"E13.filletArc"),sQuery(id+"F0.wireOp",EDGE,"E14.filletArc"),sQuery(id+"F0.wireOp",EDGE,"E15.filletArc"),sQuery(id+"F0.wireOp",EDGE,"E16.filletArc"),sQuery(id+"F0.wireOp",EDGE,"E17.filletArc"),sQuery(id+"F0.wireOp",EDGE,"E18.filletArc")])],"isStart":true});
            var sketch = newSketch(context, id + "F16", { "sketchPlane" : qUnion([Q0])});
            skLineSegment(sketch, "E56", {"start": v(80.17, 27.6) * mm, "end": v(80.17, 22.38) * mm});
            skArc(sketch, "E57", {"start": v(80.17, 32.84) * mm, "mid": v(74.94, 27.6) * mm, "end": v(80.17, 22.38) * mm});
            skLineSegment(sketch, "E58", {"start": v(80.17, 27.6) * mm, "end": v(80.17, 32.84) * mm});
            skSolve(sketch);
        }
        {
            var Q0;
            {var subQ0=sQuery(id+"F5.wireOp",EDGE,"E40");Q0=makeQuery(id+"F5.imprint","IMPRINT",FACE,{"disambiguationData":[TD([[makeQuery(id+"F5.imprint","IMPRINT",EDGE,{"derivedFrom":subQ0}),1.0]])]});}
            var Q1;
            {var subQ0=sQuery(id+"F5.wireOp",EDGE,"E39");var subQ1=sQuery(id+"F5.wireOp",EDGE,"E38");var subQ2=makeQuery(id+"F5.imprint","INTERSECT",VERTEX,{"derivedFrom":[subQ1,subQ0]});Q1=makeQuery(id+"F5.imprint","IMPRINT",FACE,{"disambiguationData":[TD([[makeQuery(id+"F5.imprint","IMPRINT",EDGE,{"disambiguationData":[TD([[subQ2,-1.0]])],"derivedFrom":subQ1}),-1.0]])]});}
            var Q2;
            Q2=sQuery(id+"F5.wireOp",EDGE,"E39");
            revolve(context, id + "F17", {"surfaceOperationType" : NewSurfaceOperationType.NEW, "entities" : qUnion([Q0, Q1]), "axis" : qUnion([Q2]), "revolveType" : RevolveType.FULL});
        }
        {
            var Q0;
            {var subQ0=sQuery(id+"F16.wireOp",EDGE,"E57");Q0=makeQuery(id+"F16.imprint","IMPRINT",FACE,{"disambiguationData":[TD([[makeQuery(id+"F16.imprint","IMPRINT",EDGE,{"derivedFrom":subQ0}),1.0]])]});}
            var Q1;
            {var subQ0=sQuery(id+"F16.wireOp",EDGE,"E58");var subQ1=sQuery(id+"F16.wireOp",EDGE,"E56");var subQ2=makeQuery(id+"F16.imprint","INTERSECT",VERTEX,{"derivedFrom":[subQ1,subQ0]});Q1=makeQuery(id+"F16.imprint","IMPRINT",FACE,{"disambiguationData":[TD([[makeQuery(id+"F16.imprint","IMPRINT",EDGE,{"disambiguationData":[TD([[subQ2,-1.0]])],"derivedFrom":subQ1}),-1.0]])]});}
            var Q2;
            Q2=sQuery(id+"F16.wireOp",EDGE,"E56");
            revolve(context, id + "F18", {"surfaceOperationType" : NewSurfaceOperationType.NEW, "entities" : qUnion([Q0, Q1]), "axis" : qUnion([Q2]), "revolveType" : RevolveType.FULL});
        }
        {
            var Q0;
            Q0=makeQuery(id+"F2.opExtrude","CAP_FACE",FACE,{"disambiguationData":[OSD([sQuery(id+"F0.wireOp",EDGE,"E0"),sQuery(id+"F0.wireOp",EDGE,"tXCEuyxa-6lNA-QPCA-4HXf-ApKYShcEb0Yf"),sQuery(id+"F0.wireOp",EDGE,"E1"),sQuery(id+"F0.wireOp",EDGE,"E2"),sQuery(id+"F0.wireOp",EDGE,"E3"),sQuery(id+"F0.wireOp",EDGE,"E4"),sQuery(id+"F0.wireOp",EDGE,"E5"),sQuery(id+"F0.wireOp",EDGE,"E6"),sQuery(id+"F0.wireOp",EDGE,"E7"),sQuery(id+"F0.wireOp",EDGE,"E8"),sQuery(id+"F0.wireOp",EDGE,"E9"),sQuery(id+"F0.wireOp",EDGE,"0kcF6Lq4-WqBE-dODE-wINV-nyZN5JArXVcS"),sQuery(id+"F0.wireOp",EDGE,"VSrMeVpB-pvXp-ETii-wjF9-Px2PqwZYQnOt"),sQuery(id+"F0.wireOp",EDGE,"OGzEMItw-FQCu-QhKJ-kTiP-AlfaDmg1CYfA"),sQuery(id+"F0.wireOp",EDGE,"E10.filletArc"),sQuery(id+"F0.wireOp",EDGE,"E11.filletArc"),sQuery(id+"F0.wireOp",EDGE,"E12.filletArc"),sQuery(id+"F0.wireOp",EDGE,"61869019-6ff7-477d-8c79-2028de4a396b.trimOffspring"),sQuery(id+"F0.wireOp",EDGE,"b39f1e7b-d492-47c6-a918-6e9c5b166b17"),sQuery(id+"F0.wireOp",EDGE,"9a7d06a7-665d-4e92-ad9d-959fca317462"),sQuery(id+"F0.wireOp",EDGE,"db31c51f-78d2-4091-9bd3-34a254103f45"),sQuery(id+"F0.wireOp",EDGE,"aaf24792-0303-4d5f-86de-c3b2a19fc74e.filletArc"),sQuery(id+"F0.wireOp",EDGE,"5ffe84d5-8cdf-4c2e-9e98-3655a6b86056.filletArc"),sQuery(id+"F0.wireOp",EDGE,"e8945d06-678d-4789-81f5-b1335d2624b7.filletArc"),sQuery(id+"F0.wireOp",EDGE,"a0b45458-2819-4e46-80a9-56e3c7e3f3b4.trimOffspring"),sQuery(id+"F0.wireOp",EDGE,"bf295548-413a-4249-b2ed-de7f7c0a0b82"),sQuery(id+"F0.wireOp",EDGE,"b03dbe81-5cdf-4ba7-a8f7-bb7ec46ab3a8"),sQuery(id+"F0.wireOp",EDGE,"b0d05724-446d-4885-847a-915c569f1139"),sQuery(id+"F0.wireOp",EDGE,"608d76ae-a745-4fd0-ae95-f5732494cd55.filletArc"),sQuery(id+"F0.wireOp",EDGE,"a41367dd-7dbd-4f08-888b-74168a8e5936.filletArc"),sQuery(id+"F0.wireOp",EDGE,"84e31002-7089-4eef-81a0-79c8965d61ed.filletArc"),sQuery(id+"F0.wireOp",EDGE,"1335fa2d-2410-4889-a90b-ae026db059b2.trimOffspring"),sQuery(id+"F0.wireOp",EDGE,"81157b49-ae94-446f-8b4e-5ce1e116e724.trimOffspring"),sQuery(id+"F0.wireOp",EDGE,"4f1c551e-3bfd-48a9-873a-6291d27f8455.trimOffspring"),sQuery(id+"F0.wireOp",EDGE,"E13.filletArc"),sQuery(id+"F0.wireOp",EDGE,"E14.filletArc"),sQuery(id+"F0.wireOp",EDGE,"E15.filletArc"),sQuery(id+"F0.wireOp",EDGE,"E16.filletArc"),sQuery(id+"F0.wireOp",EDGE,"E17.filletArc"),sQuery(id+"F0.wireOp",EDGE,"E18.filletArc")])],"isStart":true});
            var sketch = newSketch(context, id + "F19", { "sketchPlane" : qUnion([Q0])});
            skLineSegment(sketch, "E59", {"start": v(46.4, -6.9) * mm, "end": v(46.4, -12.12) * mm});
            skArc(sketch, "E60", {"start": v(46.4, -1.66) * mm, "mid": v(41.17, -6.9) * mm, "end": v(46.4, -12.12) * mm});
            skLineSegment(sketch, "E61", {"start": v(46.4, -6.9) * mm, "end": v(46.4, -1.66) * mm});
            skSolve(sketch);
        }
        {
            var Q0;
            Q0=qSketchRegion(id+"F19",true);
            var Q1;
            Q1=sQuery(id+"F19.wireOp",EDGE,"E59");
            revolve(context, id + "F20", {"surfaceOperationType" : NewSurfaceOperationType.NEW, "entities" : qUnion([Q0]), "axis" : qUnion([Q1]), "revolveType" : RevolveType.FULL});
        }
        {
            var Q0;
            Q0=makeQuery(id+"F15.opRevolve","SWEPT_BODY",BODY,{"disambiguationData":[OSD([sQuery(id+"F14.wireOp",EDGE,"E53"),sQuery(id+"F14.wireOp",EDGE,"E54"),sQuery(id+"F14.wireOp",EDGE,"E55")])]});
            var Q1;
            Q1=makeQuery(id+"F18.opRevolve","SWEPT_BODY",BODY,{"disambiguationData":[OSD([sQuery(id+"F16.wireOp",EDGE,"E56"),sQuery(id+"F16.wireOp",EDGE,"E57"),sQuery(id+"F16.wireOp",EDGE,"E58")])]});
            var Q2;
            Q2=makeQuery(id+"F13.opRevolve","SWEPT_BODY",BODY,{"disambiguationData":[OSD([sQuery(id+"F12.wireOp",EDGE,"E50"),sQuery(id+"F12.wireOp",EDGE,"E51"),sQuery(id+"F12.wireOp",EDGE,"E52")])]});
            var Q3;
            Q3=makeQuery(id+"F9.opRevolve","SWEPT_BODY",BODY,{"disambiguationData":[OSD([sQuery(id+"F8.wireOp",EDGE,"E44"),sQuery(id+"F8.wireOp",EDGE,"E45"),sQuery(id+"F8.wireOp",EDGE,"E46")])]});
            var Q4;
            Q4=makeQuery(id+"F11.opRevolve","SWEPT_BODY",BODY,{"disambiguationData":[OSD([sQuery(id+"F10.wireOp",EDGE,"E47"),sQuery(id+"F10.wireOp",EDGE,"E48"),sQuery(id+"F10.wireOp",EDGE,"E49")])]});
            var Q5;
            Q5=makeQuery(id+"F20.opRevolve","SWEPT_BODY",BODY,{"disambiguationData":[OSD([sQuery(id+"F19.wireOp",EDGE,"E59"),sQuery(id+"F19.wireOp",EDGE,"E60"),sQuery(id+"F19.wireOp",EDGE,"E61")])]});
            var Q6;
            Q6=makeQuery(id+"F17.opRevolve","SWEPT_BODY",BODY,{"disambiguationData":[OSD([sQuery(id+"F5.wireOp",EDGE,"E38"),sQuery(id+"F5.wireOp",EDGE,"E39"),sQuery(id+"F5.wireOp",EDGE,"E40")])]});
            var Q7;
            Q7=makeQuery(id+"F4.opRevolve","SWEPT_BODY",BODY,{"disambiguationData":[OSD([sQuery(id+"F3.wireOp",EDGE,"E35"),sQuery(id+"F3.wireOp",EDGE,"E36"),sQuery(id+"F3.wireOp",EDGE,"E37")])]});
            var Q8;
            Q8=makeQuery(id+"F7.opRevolve","SWEPT_BODY",BODY,{"disambiguationData":[OSD([sQuery(id+"F6.wireOp",EDGE,"E41"),sQuery(id+"F6.wireOp",EDGE,"E42"),sQuery(id+"F6.wireOp",EDGE,"E43")])]});
            var Q9;
            Q9=makeQuery(id+"F1.opExtrude","SWEPT_BODY",BODY,{"disambiguationData":[OSD([sQuery(id+"F0.wireOp",EDGE,"E0"),sQuery(id+"F0.wireOp",EDGE,"tXCEuyxa-6lNA-QPCA-4HXf-ApKYShcEb0Yf"),sQuery(id+"F0.wireOp",EDGE,"E1"),sQuery(id+"F0.wireOp",EDGE,"E2"),sQuery(id+"F0.wireOp",EDGE,"E3"),sQuery(id+"F0.wireOp",EDGE,"E4"),sQuery(id+"F0.wireOp",EDGE,"E5"),sQuery(id+"F0.wireOp",EDGE,"E6"),sQuery(id+"F0.wireOp",EDGE,"E7"),sQuery(id+"F0.wireOp",EDGE,"E8"),sQuery(id+"F0.wireOp",EDGE,"E9"),sQuery(id+"F0.wireOp",EDGE,"0kcF6Lq4-WqBE-dODE-wINV-nyZN5JArXVcS"),sQuery(id+"F0.wireOp",EDGE,"VSrMeVpB-pvXp-ETii-wjF9-Px2PqwZYQnOt"),sQuery(id+"F0.wireOp",EDGE,"OGzEMItw-FQCu-QhKJ-kTiP-AlfaDmg1CYfA"),sQuery(id+"F0.wireOp",EDGE,"E10.filletArc"),sQuery(id+"F0.wireOp",EDGE,"E11.filletArc"),sQuery(id+"F0.wireOp",EDGE,"E12.filletArc"),sQuery(id+"F0.wireOp",EDGE,"61869019-6ff7-477d-8c79-2028de4a396b.trimOffspring"),sQuery(id+"F0.wireOp",EDGE,"b39f1e7b-d492-47c6-a918-6e9c5b166b17"),sQuery(id+"F0.wireOp",EDGE,"9a7d06a7-665d-4e92-ad9d-959fca317462"),sQuery(id+"F0.wireOp",EDGE,"db31c51f-78d2-4091-9bd3-34a254103f45"),sQuery(id+"F0.wireOp",EDGE,"aaf24792-0303-4d5f-86de-c3b2a19fc74e.filletArc"),sQuery(id+"F0.wireOp",EDGE,"5ffe84d5-8cdf-4c2e-9e98-3655a6b86056.filletArc"),sQuery(id+"F0.wireOp",EDGE,"e8945d06-678d-4789-81f5-b1335d2624b7.filletArc"),sQuery(id+"F0.wireOp",EDGE,"a0b45458-2819-4e46-80a9-56e3c7e3f3b4.trimOffspring"),sQuery(id+"F0.wireOp",EDGE,"bf295548-413a-4249-b2ed-de7f7c0a0b82"),sQuery(id+"F0.wireOp",EDGE,"b03dbe81-5cdf-4ba7-a8f7-bb7ec46ab3a8"),sQuery(id+"F0.wireOp",EDGE,"b0d05724-446d-4885-847a-915c569f1139"),sQuery(id+"F0.wireOp",EDGE,"608d76ae-a745-4fd0-ae95-f5732494cd55.filletArc"),sQuery(id+"F0.wireOp",EDGE,"a41367dd-7dbd-4f08-888b-74168a8e5936.filletArc"),sQuery(id+"F0.wireOp",EDGE,"84e31002-7089-4eef-81a0-79c8965d61ed.filletArc"),sQuery(id+"F0.wireOp",EDGE,"1335fa2d-2410-4889-a90b-ae026db059b2.trimOffspring"),sQuery(id+"F0.wireOp",EDGE,"81157b49-ae94-446f-8b4e-5ce1e116e724.trimOffspring"),sQuery(id+"F0.wireOp",EDGE,"4f1c551e-3bfd-48a9-873a-6291d27f8455.trimOffspring"),sQuery(id+"F0.wireOp",EDGE,"E13.filletArc"),sQuery(id+"F0.wireOp",EDGE,"E14.filletArc"),sQuery(id+"F0.wireOp",EDGE,"E15.filletArc"),sQuery(id+"F0.wireOp",EDGE,"E16.filletArc"),sQuery(id+"F0.wireOp",EDGE,"E17.filletArc"),sQuery(id+"F0.wireOp",EDGE,"E18.filletArc")])]});
            var Q10;
            Q10=makeQuery(id+"F2.opExtrude","SWEPT_BODY",BODY,{"disambiguationData":[OSD([sQuery(id+"F0.wireOp",EDGE,"E0"),sQuery(id+"F0.wireOp",EDGE,"tXCEuyxa-6lNA-QPCA-4HXf-ApKYShcEb0Yf"),sQuery(id+"F0.wireOp",EDGE,"E1"),sQuery(id+"F0.wireOp",EDGE,"E2"),sQuery(id+"F0.wireOp",EDGE,"E3"),sQuery(id+"F0.wireOp",EDGE,"E4"),sQuery(id+"F0.wireOp",EDGE,"E5"),sQuery(id+"F0.wireOp",EDGE,"E6"),sQuery(id+"F0.wireOp",EDGE,"E7"),sQuery(id+"F0.wireOp",EDGE,"E8"),sQuery(id+"F0.wireOp",EDGE,"E9"),sQuery(id+"F0.wireOp",EDGE,"0kcF6Lq4-WqBE-dODE-wINV-nyZN5JArXVcS"),sQuery(id+"F0.wireOp",EDGE,"VSrMeVpB-pvXp-ETii-wjF9-Px2PqwZYQnOt"),sQuery(id+"F0.wireOp",EDGE,"OGzEMItw-FQCu-QhKJ-kTiP-AlfaDmg1CYfA"),sQuery(id+"F0.wireOp",EDGE,"E10.filletArc"),sQuery(id+"F0.wireOp",EDGE,"E11.filletArc"),sQuery(id+"F0.wireOp",EDGE,"E12.filletArc"),sQuery(id+"F0.wireOp",EDGE,"61869019-6ff7-477d-8c79-2028de4a396b.trimOffspring"),sQuery(id+"F0.wireOp",EDGE,"b39f1e7b-d492-47c6-a918-6e9c5b166b17"),sQuery(id+"F0.wireOp",EDGE,"9a7d06a7-665d-4e92-ad9d-959fca317462"),sQuery(id+"F0.wireOp",EDGE,"db31c51f-78d2-4091-9bd3-34a254103f45"),sQuery(id+"F0.wireOp",EDGE,"aaf24792-0303-4d5f-86de-c3b2a19fc74e.filletArc"),sQuery(id+"F0.wireOp",EDGE,"5ffe84d5-8cdf-4c2e-9e98-3655a6b86056.filletArc"),sQuery(id+"F0.wireOp",EDGE,"e8945d06-678d-4789-81f5-b1335d2624b7.filletArc"),sQuery(id+"F0.wireOp",EDGE,"a0b45458-2819-4e46-80a9-56e3c7e3f3b4.trimOffspring"),sQuery(id+"F0.wireOp",EDGE,"bf295548-413a-4249-b2ed-de7f7c0a0b82"),sQuery(id+"F0.wireOp",EDGE,"b03dbe81-5cdf-4ba7-a8f7-bb7ec46ab3a8"),sQuery(id+"F0.wireOp",EDGE,"b0d05724-446d-4885-847a-915c569f1139"),sQuery(id+"F0.wireOp",EDGE,"608d76ae-a745-4fd0-ae95-f5732494cd55.filletArc"),sQuery(id+"F0.wireOp",EDGE,"a41367dd-7dbd-4f08-888b-74168a8e5936.filletArc"),sQuery(id+"F0.wireOp",EDGE,"84e31002-7089-4eef-81a0-79c8965d61ed.filletArc"),sQuery(id+"F0.wireOp",EDGE,"1335fa2d-2410-4889-a90b-ae026db059b2.trimOffspring"),sQuery(id+"F0.wireOp",EDGE,"81157b49-ae94-446f-8b4e-5ce1e116e724.trimOffspring"),sQuery(id+"F0.wireOp",EDGE,"4f1c551e-3bfd-48a9-873a-6291d27f8455.trimOffspring"),sQuery(id+"F0.wireOp",EDGE,"E13.filletArc"),sQuery(id+"F0.wireOp",EDGE,"E14.filletArc"),sQuery(id+"F0.wireOp",EDGE,"E15.filletArc"),sQuery(id+"F0.wireOp",EDGE,"E16.filletArc"),sQuery(id+"F0.wireOp",EDGE,"E17.filletArc"),sQuery(id+"F0.wireOp",EDGE,"E18.filletArc")])]});
            booleanBodies(context, id + "F21", {"operationType" : BooleanOperationType.SUBTRACTION, "tools" : qUnion([Q0, Q1, Q2, Q3, Q4, Q5, Q6, Q7, Q8]), "targets" : qUnion([Q9, Q10])});
        }
        {
            var Q0;
            Q0=makeQuery(id+"F2.opExtrude","CAP_FACE",FACE,{"disambiguationData":[OSD([sQuery(id+"F0.wireOp",EDGE,"E0"),sQuery(id+"F0.wireOp",EDGE,"tXCEuyxa-6lNA-QPCA-4HXf-ApKYShcEb0Yf"),sQuery(id+"F0.wireOp",EDGE,"E1"),sQuery(id+"F0.wireOp",EDGE,"E2"),sQuery(id+"F0.wireOp",EDGE,"E3"),sQuery(id+"F0.wireOp",EDGE,"E4"),sQuery(id+"F0.wireOp",EDGE,"E5"),sQuery(id+"F0.wireOp",EDGE,"E6"),sQuery(id+"F0.wireOp",EDGE,"E7"),sQuery(id+"F0.wireOp",EDGE,"E8"),sQuery(id+"F0.wireOp",EDGE,"E9"),sQuery(id+"F0.wireOp",EDGE,"0kcF6Lq4-WqBE-dODE-wINV-nyZN5JArXVcS"),sQuery(id+"F0.wireOp",EDGE,"VSrMeVpB-pvXp-ETii-wjF9-Px2PqwZYQnOt"),sQuery(id+"F0.wireOp",EDGE,"OGzEMItw-FQCu-QhKJ-kTiP-AlfaDmg1CYfA"),sQuery(id+"F0.wireOp",EDGE,"E10.filletArc"),sQuery(id+"F0.wireOp",EDGE,"E11.filletArc"),sQuery(id+"F0.wireOp",EDGE,"E12.filletArc"),sQuery(id+"F0.wireOp",EDGE,"61869019-6ff7-477d-8c79-2028de4a396b.trimOffspring"),sQuery(id+"F0.wireOp",EDGE,"b39f1e7b-d492-47c6-a918-6e9c5b166b17"),sQuery(id+"F0.wireOp",EDGE,"9a7d06a7-665d-4e92-ad9d-959fca317462"),sQuery(id+"F0.wireOp",EDGE,"db31c51f-78d2-4091-9bd3-34a254103f45"),sQuery(id+"F0.wireOp",EDGE,"aaf24792-0303-4d5f-86de-c3b2a19fc74e.filletArc"),sQuery(id+"F0.wireOp",EDGE,"5ffe84d5-8cdf-4c2e-9e98-3655a6b86056.filletArc"),sQuery(id+"F0.wireOp",EDGE,"e8945d06-678d-4789-81f5-b1335d2624b7.filletArc"),sQuery(id+"F0.wireOp",EDGE,"a0b45458-2819-4e46-80a9-56e3c7e3f3b4.trimOffspring"),sQuery(id+"F0.wireOp",EDGE,"bf295548-413a-4249-b2ed-de7f7c0a0b82"),sQuery(id+"F0.wireOp",EDGE,"b03dbe81-5cdf-4ba7-a8f7-bb7ec46ab3a8"),sQuery(id+"F0.wireOp",EDGE,"b0d05724-446d-4885-847a-915c569f1139"),sQuery(id+"F0.wireOp",EDGE,"608d76ae-a745-4fd0-ae95-f5732494cd55.filletArc"),sQuery(id+"F0.wireOp",EDGE,"a41367dd-7dbd-4f08-888b-74168a8e5936.filletArc"),sQuery(id+"F0.wireOp",EDGE,"84e31002-7089-4eef-81a0-79c8965d61ed.filletArc"),sQuery(id+"F0.wireOp",EDGE,"1335fa2d-2410-4889-a90b-ae026db059b2.trimOffspring"),sQuery(id+"F0.wireOp",EDGE,"81157b49-ae94-446f-8b4e-5ce1e116e724.trimOffspring"),sQuery(id+"F0.wireOp",EDGE,"4f1c551e-3bfd-48a9-873a-6291d27f8455.trimOffspring"),sQuery(id+"F0.wireOp",EDGE,"E13.filletArc"),sQuery(id+"F0.wireOp",EDGE,"E14.filletArc"),sQuery(id+"F0.wireOp",EDGE,"E15.filletArc"),sQuery(id+"F0.wireOp",EDGE,"E16.filletArc"),sQuery(id+"F0.wireOp",EDGE,"E17.filletArc"),sQuery(id+"F0.wireOp",EDGE,"E18.filletArc")])],"isStart":false});
            var sketch = newSketch(context, id + "F22", { "sketchPlane" : qUnion([Q0])});
            skCircle(sketch, "E62", {"center": v(73.24, -0.6) * mm, "radius": 5.39 * mm});
            skSolve(sketch);
        }
        {
            var Q0;
            Q0=makeQuery(id+"F22.imprint","IMPRINT",FACE,{"disambiguationData":[TD([[makeQuery(id+"F22.imprint","IMPRINT",EDGE,{"derivedFrom":sQuery(id+"F22.wireOp",EDGE,"E62")}),-1.0]])]});
            extrude(context, id + "F23", {"entities" : qUnion([Q0]), "oppositeDirection" : true, "depth" : 1 * mm, "offsetDistance" : 25 * mm});
        }
        {
            var Q0;
            Q0=makeQuery(id+"F1.opExtrude","CAP_EDGE",EDGE,{"disambiguationData":[OSD([sQuery(id+"F0.wireOp",EDGE,"E19.14")])],"isStart":false});
            var Q1;
            Q1=makeQuery(id+"F2.opExtrude","CAP_EDGE",EDGE,{"disambiguationData":[OSD([sQuery(id+"F0.wireOp",EDGE,"E19.14")])],"isStart":false});
            fillet(context, id + "F24", {"entities" : qUnion([Q0, Q1]), "radius" : 1.7 * mm, "tangentPropagation" : true, "allowEdgeOverflow" : false});
        }
        {
            var Q0;
            Q0=makeQuery(id+"F1.opExtrude","CAP_EDGE",EDGE,{"disambiguationData":[OSD([sQuery(id+"F0.wireOp",EDGE,"E0")])],"isStart":false});
            fillet(context, id + "F25", {"entities" : qUnion([Q0]), "radius" : .6 * mm, "tangentPropagation" : true, "allowEdgeOverflow" : false});
        }
        {
            var Q0;
            Q0=makeQuery(id+"F21.opBoolean","INTERSECT",EDGE,{"derivedFrom":[makeQuery(id+"F1.opExtrude","CAP_FACE",FACE,{"disambiguationData":[OSD([sQuery(id+"F0.wireOp",EDGE,"E0"),sQuery(id+"F0.wireOp",EDGE,"E1"),sQuery(id+"F0.wireOp",EDGE,"E2"),sQuery(id+"F0.wireOp",EDGE,"E3"),sQuery(id+"F0.wireOp",EDGE,"E4"),sQuery(id+"F0.wireOp",EDGE,"E5"),sQuery(id+"F0.wireOp",EDGE,"E6"),sQuery(id+"F0.wireOp",EDGE,"E7"),sQuery(id+"F0.wireOp",EDGE,"E8"),sQuery(id+"F0.wireOp",EDGE,"E9"),sQuery(id+"F0.wireOp",EDGE,"E19.0"),sQuery(id+"F0.wireOp",EDGE,"E19.1"),sQuery(id+"F0.wireOp",EDGE,"E19.2"),sQuery(id+"F0.wireOp",EDGE,"E19.3"),sQuery(id+"F0.wireOp",EDGE,"E19.4"),sQuery(id+"F0.wireOp",EDGE,"E19.5"),sQuery(id+"F0.wireOp",EDGE,"E19.6"),sQuery(id+"F0.wireOp",EDGE,"E19.7"),sQuery(id+"F0.wireOp",EDGE,"E19.8"),sQuery(id+"F0.wireOp",EDGE,"E19.9"),sQuery(id+"F0.wireOp",EDGE,"E19.10"),sQuery(id+"F0.wireOp",EDGE,"E19.11"),sQuery(id+"F0.wireOp",EDGE,"E19.12"),sQuery(id+"F0.wireOp",EDGE,"E19.13"),sQuery(id+"F0.wireOp",EDGE,"E19.14"),sQuery(id+"F0.wireOp",EDGE,"E20.0"),sQuery(id+"F0.wireOp",EDGE,"E21.0"),sQuery(id+"F0.wireOp",EDGE,"E22.0"),sQuery(id+"F0.wireOp",EDGE,"E23.0"),sQuery(id+"F0.wireOp",EDGE,"E24.0"),sQuery(id+"F0.wireOp",EDGE,"E25.0"),sQuery(id+"F0.wireOp",EDGE,"E26.0"),sQuery(id+"F0.wireOp",EDGE,"E27.0"),sQuery(id+"F0.wireOp",EDGE,"E28.0"),sQuery(id+"F0.wireOp",EDGE,"E29.0"),sQuery(id+"F0.wireOp",EDGE,"E30.0"),sQuery(id+"F0.wireOp",EDGE,"E31.0"),sQuery(id+"F0.wireOp",EDGE,"E32.0"),sQuery(id+"F0.wireOp",EDGE,"E33.0"),sQuery(id+"F0.wireOp",EDGE,"E34.0")])],"isStart":false}),makeQuery(id+"F7.opRevolve","SWEPT_FACE",FACE,{"disambiguationData":[OSD([sQuery(id+"F6.wireOp",EDGE,"E42")])]})]});
            var Q1;
            Q1=makeQuery(id+"F21.opBoolean","INTERSECT",EDGE,{"derivedFrom":[makeQuery(id+"F1.opExtrude","CAP_FACE",FACE,{"disambiguationData":[OSD([sQuery(id+"F0.wireOp",EDGE,"E0"),sQuery(id+"F0.wireOp",EDGE,"E1"),sQuery(id+"F0.wireOp",EDGE,"E2"),sQuery(id+"F0.wireOp",EDGE,"E3"),sQuery(id+"F0.wireOp",EDGE,"E4"),sQuery(id+"F0.wireOp",EDGE,"E5"),sQuery(id+"F0.wireOp",EDGE,"E6"),sQuery(id+"F0.wireOp",EDGE,"E7"),sQuery(id+"F0.wireOp",EDGE,"E8"),sQuery(id+"F0.wireOp",EDGE,"E9"),sQuery(id+"F0.wireOp",EDGE,"E19.0"),sQuery(id+"F0.wireOp",EDGE,"E19.1"),sQuery(id+"F0.wireOp",EDGE,"E19.2"),sQuery(id+"F0.wireOp",EDGE,"E19.3"),sQuery(id+"F0.wireOp",EDGE,"E19.4"),sQuery(id+"F0.wireOp",EDGE,"E19.5"),sQuery(id+"F0.wireOp",EDGE,"E19.6"),sQuery(id+"F0.wireOp",EDGE,"E19.7"),sQuery(id+"F0.wireOp",EDGE,"E19.8"),sQuery(id+"F0.wireOp",EDGE,"E19.9"),sQuery(id+"F0.wireOp",EDGE,"E19.10"),sQuery(id+"F0.wireOp",EDGE,"E19.11"),sQuery(id+"F0.wireOp",EDGE,"E19.12"),sQuery(id+"F0.wireOp",EDGE,"E19.13"),sQuery(id+"F0.wireOp",EDGE,"E19.14"),sQuery(id+"F0.wireOp",EDGE,"E20.0"),sQuery(id+"F0.wireOp",EDGE,"E21.0"),sQuery(id+"F0.wireOp",EDGE,"E22.0"),sQuery(id+"F0.wireOp",EDGE,"E23.0"),sQuery(id+"F0.wireOp",EDGE,"E24.0"),sQuery(id+"F0.wireOp",EDGE,"E25.0"),sQuery(id+"F0.wireOp",EDGE,"E26.0"),sQuery(id+"F0.wireOp",EDGE,"E27.0"),sQuery(id+"F0.wireOp",EDGE,"E28.0"),sQuery(id+"F0.wireOp",EDGE,"E29.0"),sQuery(id+"F0.wireOp",EDGE,"E30.0"),sQuery(id+"F0.wireOp",EDGE,"E31.0"),sQuery(id+"F0.wireOp",EDGE,"E32.0"),sQuery(id+"F0.wireOp",EDGE,"E33.0"),sQuery(id+"F0.wireOp",EDGE,"E34.0")])],"isStart":false}),makeQuery(id+"F9.opRevolve","SWEPT_FACE",FACE,{"disambiguationData":[OSD([sQuery(id+"F8.wireOp",EDGE,"E45")])]})]});
            var Q2;
            Q2=makeQuery(id+"F21.opBoolean","INTERSECT",EDGE,{"derivedFrom":[makeQuery(id+"F1.opExtrude","CAP_FACE",FACE,{"disambiguationData":[OSD([sQuery(id+"F0.wireOp",EDGE,"E0"),sQuery(id+"F0.wireOp",EDGE,"E1"),sQuery(id+"F0.wireOp",EDGE,"E2"),sQuery(id+"F0.wireOp",EDGE,"E3"),sQuery(id+"F0.wireOp",EDGE,"E4"),sQuery(id+"F0.wireOp",EDGE,"E5"),sQuery(id+"F0.wireOp",EDGE,"E6"),sQuery(id+"F0.wireOp",EDGE,"E7"),sQuery(id+"F0.wireOp",EDGE,"E8"),sQuery(id+"F0.wireOp",EDGE,"E9"),sQuery(id+"F0.wireOp",EDGE,"E19.0"),sQuery(id+"F0.wireOp",EDGE,"E19.1"),sQuery(id+"F0.wireOp",EDGE,"E19.2"),sQuery(id+"F0.wireOp",EDGE,"E19.3"),sQuery(id+"F0.wireOp",EDGE,"E19.4"),sQuery(id+"F0.wireOp",EDGE,"E19.5"),sQuery(id+"F0.wireOp",EDGE,"E19.6"),sQuery(id+"F0.wireOp",EDGE,"E19.7"),sQuery(id+"F0.wireOp",EDGE,"E19.8"),sQuery(id+"F0.wireOp",EDGE,"E19.9"),sQuery(id+"F0.wireOp",EDGE,"E19.10"),sQuery(id+"F0.wireOp",EDGE,"E19.11"),sQuery(id+"F0.wireOp",EDGE,"E19.12"),sQuery(id+"F0.wireOp",EDGE,"E19.13"),sQuery(id+"F0.wireOp",EDGE,"E19.14"),sQuery(id+"F0.wireOp",EDGE,"E20.0"),sQuery(id+"F0.wireOp",EDGE,"E21.0"),sQuery(id+"F0.wireOp",EDGE,"E22.0"),sQuery(id+"F0.wireOp",EDGE,"E23.0"),sQuery(id+"F0.wireOp",EDGE,"E24.0"),sQuery(id+"F0.wireOp",EDGE,"E25.0"),sQuery(id+"F0.wireOp",EDGE,"E26.0"),sQuery(id+"F0.wireOp",EDGE,"E27.0"),sQuery(id+"F0.wireOp",EDGE,"E28.0"),sQuery(id+"F0.wireOp",EDGE,"E29.0"),sQuery(id+"F0.wireOp",EDGE,"E30.0"),sQuery(id+"F0.wireOp",EDGE,"E31.0"),sQuery(id+"F0.wireOp",EDGE,"E32.0"),sQuery(id+"F0.wireOp",EDGE,"E33.0"),sQuery(id+"F0.wireOp",EDGE,"E34.0")])],"isStart":false}),makeQuery(id+"F11.opRevolve","SWEPT_FACE",FACE,{"disambiguationData":[OSD([sQuery(id+"F10.wireOp",EDGE,"E48")])]})]});
            var Q3;
            Q3=makeQuery(id+"F21.opBoolean","INTERSECT",EDGE,{"derivedFrom":[makeQuery(id+"F1.opExtrude","CAP_FACE",FACE,{"disambiguationData":[OSD([sQuery(id+"F0.wireOp",EDGE,"E0"),sQuery(id+"F0.wireOp",EDGE,"E1"),sQuery(id+"F0.wireOp",EDGE,"E2"),sQuery(id+"F0.wireOp",EDGE,"E3"),sQuery(id+"F0.wireOp",EDGE,"E4"),sQuery(id+"F0.wireOp",EDGE,"E5"),sQuery(id+"F0.wireOp",EDGE,"E6"),sQuery(id+"F0.wireOp",EDGE,"E7"),sQuery(id+"F0.wireOp",EDGE,"E8"),sQuery(id+"F0.wireOp",EDGE,"E9"),sQuery(id+"F0.wireOp",EDGE,"E19.0"),sQuery(id+"F0.wireOp",EDGE,"E19.1"),sQuery(id+"F0.wireOp",EDGE,"E19.2"),sQuery(id+"F0.wireOp",EDGE,"E19.3"),sQuery(id+"F0.wireOp",EDGE,"E19.4"),sQuery(id+"F0.wireOp",EDGE,"E19.5"),sQuery(id+"F0.wireOp",EDGE,"E19.6"),sQuery(id+"F0.wireOp",EDGE,"E19.7"),sQuery(id+"F0.wireOp",EDGE,"E19.8"),sQuery(id+"F0.wireOp",EDGE,"E19.9"),sQuery(id+"F0.wireOp",EDGE,"E19.10"),sQuery(id+"F0.wireOp",EDGE,"E19.11"),sQuery(id+"F0.wireOp",EDGE,"E19.12"),sQuery(id+"F0.wireOp",EDGE,"E19.13"),sQuery(id+"F0.wireOp",EDGE,"E19.14"),sQuery(id+"F0.wireOp",EDGE,"E20.0"),sQuery(id+"F0.wireOp",EDGE,"E21.0"),sQuery(id+"F0.wireOp",EDGE,"E22.0"),sQuery(id+"F0.wireOp",EDGE,"E23.0"),sQuery(id+"F0.wireOp",EDGE,"E24.0"),sQuery(id+"F0.wireOp",EDGE,"E25.0"),sQuery(id+"F0.wireOp",EDGE,"E26.0"),sQuery(id+"F0.wireOp",EDGE,"E27.0"),sQuery(id+"F0.wireOp",EDGE,"E28.0"),sQuery(id+"F0.wireOp",EDGE,"E29.0"),sQuery(id+"F0.wireOp",EDGE,"E30.0"),sQuery(id+"F0.wireOp",EDGE,"E31.0"),sQuery(id+"F0.wireOp",EDGE,"E32.0"),sQuery(id+"F0.wireOp",EDGE,"E33.0"),sQuery(id+"F0.wireOp",EDGE,"E34.0")])],"isStart":false}),makeQuery(id+"F4.opRevolve","SWEPT_FACE",FACE,{"disambiguationData":[OSD([sQuery(id+"F3.wireOp",EDGE,"E37")])]})]});
            var Q4;
            Q4=makeQuery(id+"F21.opBoolean","INTERSECT",EDGE,{"derivedFrom":[makeQuery(id+"F1.opExtrude","CAP_FACE",FACE,{"disambiguationData":[OSD([sQuery(id+"F0.wireOp",EDGE,"E0"),sQuery(id+"F0.wireOp",EDGE,"E1"),sQuery(id+"F0.wireOp",EDGE,"E2"),sQuery(id+"F0.wireOp",EDGE,"E3"),sQuery(id+"F0.wireOp",EDGE,"E4"),sQuery(id+"F0.wireOp",EDGE,"E5"),sQuery(id+"F0.wireOp",EDGE,"E6"),sQuery(id+"F0.wireOp",EDGE,"E7"),sQuery(id+"F0.wireOp",EDGE,"E8"),sQuery(id+"F0.wireOp",EDGE,"E9"),sQuery(id+"F0.wireOp",EDGE,"E19.0"),sQuery(id+"F0.wireOp",EDGE,"E19.1"),sQuery(id+"F0.wireOp",EDGE,"E19.2"),sQuery(id+"F0.wireOp",EDGE,"E19.3"),sQuery(id+"F0.wireOp",EDGE,"E19.4"),sQuery(id+"F0.wireOp",EDGE,"E19.5"),sQuery(id+"F0.wireOp",EDGE,"E19.6"),sQuery(id+"F0.wireOp",EDGE,"E19.7"),sQuery(id+"F0.wireOp",EDGE,"E19.8"),sQuery(id+"F0.wireOp",EDGE,"E19.9"),sQuery(id+"F0.wireOp",EDGE,"E19.10"),sQuery(id+"F0.wireOp",EDGE,"E19.11"),sQuery(id+"F0.wireOp",EDGE,"E19.12"),sQuery(id+"F0.wireOp",EDGE,"E19.13"),sQuery(id+"F0.wireOp",EDGE,"E19.14"),sQuery(id+"F0.wireOp",EDGE,"E20.0"),sQuery(id+"F0.wireOp",EDGE,"E21.0"),sQuery(id+"F0.wireOp",EDGE,"E22.0"),sQuery(id+"F0.wireOp",EDGE,"E23.0"),sQuery(id+"F0.wireOp",EDGE,"E24.0"),sQuery(id+"F0.wireOp",EDGE,"E25.0"),sQuery(id+"F0.wireOp",EDGE,"E26.0"),sQuery(id+"F0.wireOp",EDGE,"E27.0"),sQuery(id+"F0.wireOp",EDGE,"E28.0"),sQuery(id+"F0.wireOp",EDGE,"E29.0"),sQuery(id+"F0.wireOp",EDGE,"E30.0"),sQuery(id+"F0.wireOp",EDGE,"E31.0"),sQuery(id+"F0.wireOp",EDGE,"E32.0"),sQuery(id+"F0.wireOp",EDGE,"E33.0"),sQuery(id+"F0.wireOp",EDGE,"E34.0")])],"isStart":false}),makeQuery(id+"F20.opRevolve","SWEPT_FACE",FACE,{"disambiguationData":[OSD([sQuery(id+"F19.wireOp",EDGE,"E60")])]})]});
            var Q5;
            Q5=makeQuery(id+"F21.opBoolean","INTERSECT",EDGE,{"derivedFrom":[makeQuery(id+"F1.opExtrude","CAP_FACE",FACE,{"disambiguationData":[OSD([sQuery(id+"F0.wireOp",EDGE,"E0"),sQuery(id+"F0.wireOp",EDGE,"E1"),sQuery(id+"F0.wireOp",EDGE,"E2"),sQuery(id+"F0.wireOp",EDGE,"E3"),sQuery(id+"F0.wireOp",EDGE,"E4"),sQuery(id+"F0.wireOp",EDGE,"E5"),sQuery(id+"F0.wireOp",EDGE,"E6"),sQuery(id+"F0.wireOp",EDGE,"E7"),sQuery(id+"F0.wireOp",EDGE,"E8"),sQuery(id+"F0.wireOp",EDGE,"E9"),sQuery(id+"F0.wireOp",EDGE,"E19.0"),sQuery(id+"F0.wireOp",EDGE,"E19.1"),sQuery(id+"F0.wireOp",EDGE,"E19.2"),sQuery(id+"F0.wireOp",EDGE,"E19.3"),sQuery(id+"F0.wireOp",EDGE,"E19.4"),sQuery(id+"F0.wireOp",EDGE,"E19.5"),sQuery(id+"F0.wireOp",EDGE,"E19.6"),sQuery(id+"F0.wireOp",EDGE,"E19.7"),sQuery(id+"F0.wireOp",EDGE,"E19.8"),sQuery(id+"F0.wireOp",EDGE,"E19.9"),sQuery(id+"F0.wireOp",EDGE,"E19.10"),sQuery(id+"F0.wireOp",EDGE,"E19.11"),sQuery(id+"F0.wireOp",EDGE,"E19.12"),sQuery(id+"F0.wireOp",EDGE,"E19.13"),sQuery(id+"F0.wireOp",EDGE,"E19.14"),sQuery(id+"F0.wireOp",EDGE,"E20.0"),sQuery(id+"F0.wireOp",EDGE,"E21.0"),sQuery(id+"F0.wireOp",EDGE,"E22.0"),sQuery(id+"F0.wireOp",EDGE,"E23.0"),sQuery(id+"F0.wireOp",EDGE,"E24.0"),sQuery(id+"F0.wireOp",EDGE,"E25.0"),sQuery(id+"F0.wireOp",EDGE,"E26.0"),sQuery(id+"F0.wireOp",EDGE,"E27.0"),sQuery(id+"F0.wireOp",EDGE,"E28.0"),sQuery(id+"F0.wireOp",EDGE,"E29.0"),sQuery(id+"F0.wireOp",EDGE,"E30.0"),sQuery(id+"F0.wireOp",EDGE,"E31.0"),sQuery(id+"F0.wireOp",EDGE,"E32.0"),sQuery(id+"F0.wireOp",EDGE,"E33.0"),sQuery(id+"F0.wireOp",EDGE,"E34.0")])],"isStart":false}),makeQuery(id+"F17.opRevolve","SWEPT_FACE",FACE,{"disambiguationData":[OSD([sQuery(id+"F5.wireOp",EDGE,"E40")])]})]});
            var Q6;
            Q6=makeQuery(id+"F21.opBoolean","INTERSECT",EDGE,{"derivedFrom":[makeQuery(id+"F1.opExtrude","CAP_FACE",FACE,{"disambiguationData":[OSD([sQuery(id+"F0.wireOp",EDGE,"E0"),sQuery(id+"F0.wireOp",EDGE,"E1"),sQuery(id+"F0.wireOp",EDGE,"E2"),sQuery(id+"F0.wireOp",EDGE,"E3"),sQuery(id+"F0.wireOp",EDGE,"E4"),sQuery(id+"F0.wireOp",EDGE,"E5"),sQuery(id+"F0.wireOp",EDGE,"E6"),sQuery(id+"F0.wireOp",EDGE,"E7"),sQuery(id+"F0.wireOp",EDGE,"E8"),sQuery(id+"F0.wireOp",EDGE,"E9"),sQuery(id+"F0.wireOp",EDGE,"E19.0"),sQuery(id+"F0.wireOp",EDGE,"E19.1"),sQuery(id+"F0.wireOp",EDGE,"E19.2"),sQuery(id+"F0.wireOp",EDGE,"E19.3"),sQuery(id+"F0.wireOp",EDGE,"E19.4"),sQuery(id+"F0.wireOp",EDGE,"E19.5"),sQuery(id+"F0.wireOp",EDGE,"E19.6"),sQuery(id+"F0.wireOp",EDGE,"E19.7"),sQuery(id+"F0.wireOp",EDGE,"E19.8"),sQuery(id+"F0.wireOp",EDGE,"E19.9"),sQuery(id+"F0.wireOp",EDGE,"E19.10"),sQuery(id+"F0.wireOp",EDGE,"E19.11"),sQuery(id+"F0.wireOp",EDGE,"E19.12"),sQuery(id+"F0.wireOp",EDGE,"E19.13"),sQuery(id+"F0.wireOp",EDGE,"E19.14"),sQuery(id+"F0.wireOp",EDGE,"E20.0"),sQuery(id+"F0.wireOp",EDGE,"E21.0"),sQuery(id+"F0.wireOp",EDGE,"E22.0"),sQuery(id+"F0.wireOp",EDGE,"E23.0"),sQuery(id+"F0.wireOp",EDGE,"E24.0"),sQuery(id+"F0.wireOp",EDGE,"E25.0"),sQuery(id+"F0.wireOp",EDGE,"E26.0"),sQuery(id+"F0.wireOp",EDGE,"E27.0"),sQuery(id+"F0.wireOp",EDGE,"E28.0"),sQuery(id+"F0.wireOp",EDGE,"E29.0"),sQuery(id+"F0.wireOp",EDGE,"E30.0"),sQuery(id+"F0.wireOp",EDGE,"E31.0"),sQuery(id+"F0.wireOp",EDGE,"E32.0"),sQuery(id+"F0.wireOp",EDGE,"E33.0"),sQuery(id+"F0.wireOp",EDGE,"E34.0")])],"isStart":false}),makeQuery(id+"F13.opRevolve","SWEPT_FACE",FACE,{"disambiguationData":[OSD([sQuery(id+"F12.wireOp",EDGE,"E51")])]})]});
            var Q7;
            Q7=makeQuery(id+"F21.opBoolean","INTERSECT",EDGE,{"derivedFrom":[makeQuery(id+"F1.opExtrude","CAP_FACE",FACE,{"disambiguationData":[OSD([sQuery(id+"F0.wireOp",EDGE,"E0"),sQuery(id+"F0.wireOp",EDGE,"E1"),sQuery(id+"F0.wireOp",EDGE,"E2"),sQuery(id+"F0.wireOp",EDGE,"E3"),sQuery(id+"F0.wireOp",EDGE,"E4"),sQuery(id+"F0.wireOp",EDGE,"E5"),sQuery(id+"F0.wireOp",EDGE,"E6"),sQuery(id+"F0.wireOp",EDGE,"E7"),sQuery(id+"F0.wireOp",EDGE,"E8"),sQuery(id+"F0.wireOp",EDGE,"E9"),sQuery(id+"F0.wireOp",EDGE,"E19.0"),sQuery(id+"F0.wireOp",EDGE,"E19.1"),sQuery(id+"F0.wireOp",EDGE,"E19.2"),sQuery(id+"F0.wireOp",EDGE,"E19.3"),sQuery(id+"F0.wireOp",EDGE,"E19.4"),sQuery(id+"F0.wireOp",EDGE,"E19.5"),sQuery(id+"F0.wireOp",EDGE,"E19.6"),sQuery(id+"F0.wireOp",EDGE,"E19.7"),sQuery(id+"F0.wireOp",EDGE,"E19.8"),sQuery(id+"F0.wireOp",EDGE,"E19.9"),sQuery(id+"F0.wireOp",EDGE,"E19.10"),sQuery(id+"F0.wireOp",EDGE,"E19.11"),sQuery(id+"F0.wireOp",EDGE,"E19.12"),sQuery(id+"F0.wireOp",EDGE,"E19.13"),sQuery(id+"F0.wireOp",EDGE,"E19.14"),sQuery(id+"F0.wireOp",EDGE,"E20.0"),sQuery(id+"F0.wireOp",EDGE,"E21.0"),sQuery(id+"F0.wireOp",EDGE,"E22.0"),sQuery(id+"F0.wireOp",EDGE,"E23.0"),sQuery(id+"F0.wireOp",EDGE,"E24.0"),sQuery(id+"F0.wireOp",EDGE,"E25.0"),sQuery(id+"F0.wireOp",EDGE,"E26.0"),sQuery(id+"F0.wireOp",EDGE,"E27.0"),sQuery(id+"F0.wireOp",EDGE,"E28.0"),sQuery(id+"F0.wireOp",EDGE,"E29.0"),sQuery(id+"F0.wireOp",EDGE,"E30.0"),sQuery(id+"F0.wireOp",EDGE,"E31.0"),sQuery(id+"F0.wireOp",EDGE,"E32.0"),sQuery(id+"F0.wireOp",EDGE,"E33.0"),sQuery(id+"F0.wireOp",EDGE,"E34.0")])],"isStart":false}),makeQuery(id+"F15.opRevolve","SWEPT_FACE",FACE,{"disambiguationData":[OSD([sQuery(id+"F14.wireOp",EDGE,"E54")])]})]});
            var Q8;
            Q8=makeQuery(id+"F21.opBoolean","INTERSECT",EDGE,{"derivedFrom":[makeQuery(id+"F1.opExtrude","CAP_FACE",FACE,{"disambiguationData":[OSD([sQuery(id+"F0.wireOp",EDGE,"E0"),sQuery(id+"F0.wireOp",EDGE,"E1"),sQuery(id+"F0.wireOp",EDGE,"E2"),sQuery(id+"F0.wireOp",EDGE,"E3"),sQuery(id+"F0.wireOp",EDGE,"E4"),sQuery(id+"F0.wireOp",EDGE,"E5"),sQuery(id+"F0.wireOp",EDGE,"E6"),sQuery(id+"F0.wireOp",EDGE,"E7"),sQuery(id+"F0.wireOp",EDGE,"E8"),sQuery(id+"F0.wireOp",EDGE,"E9"),sQuery(id+"F0.wireOp",EDGE,"E19.0"),sQuery(id+"F0.wireOp",EDGE,"E19.1"),sQuery(id+"F0.wireOp",EDGE,"E19.2"),sQuery(id+"F0.wireOp",EDGE,"E19.3"),sQuery(id+"F0.wireOp",EDGE,"E19.4"),sQuery(id+"F0.wireOp",EDGE,"E19.5"),sQuery(id+"F0.wireOp",EDGE,"E19.6"),sQuery(id+"F0.wireOp",EDGE,"E19.7"),sQuery(id+"F0.wireOp",EDGE,"E19.8"),sQuery(id+"F0.wireOp",EDGE,"E19.9"),sQuery(id+"F0.wireOp",EDGE,"E19.10"),sQuery(id+"F0.wireOp",EDGE,"E19.11"),sQuery(id+"F0.wireOp",EDGE,"E19.12"),sQuery(id+"F0.wireOp",EDGE,"E19.13"),sQuery(id+"F0.wireOp",EDGE,"E19.14"),sQuery(id+"F0.wireOp",EDGE,"E20.0"),sQuery(id+"F0.wireOp",EDGE,"E21.0"),sQuery(id+"F0.wireOp",EDGE,"E22.0"),sQuery(id+"F0.wireOp",EDGE,"E23.0"),sQuery(id+"F0.wireOp",EDGE,"E24.0"),sQuery(id+"F0.wireOp",EDGE,"E25.0"),sQuery(id+"F0.wireOp",EDGE,"E26.0"),sQuery(id+"F0.wireOp",EDGE,"E27.0"),sQuery(id+"F0.wireOp",EDGE,"E28.0"),sQuery(id+"F0.wireOp",EDGE,"E29.0"),sQuery(id+"F0.wireOp",EDGE,"E30.0"),sQuery(id+"F0.wireOp",EDGE,"E31.0"),sQuery(id+"F0.wireOp",EDGE,"E32.0"),sQuery(id+"F0.wireOp",EDGE,"E33.0"),sQuery(id+"F0.wireOp",EDGE,"E34.0")])],"isStart":false}),makeQuery(id+"F18.opRevolve","SWEPT_FACE",FACE,{"disambiguationData":[OSD([sQuery(id+"F16.wireOp",EDGE,"E57")])]})]});
            var Q9;
            Q9=makeQuery(id+"F21.opBoolean","INTERSECT",EDGE,{"derivedFrom":[makeQuery(id+"F2.opExtrude","CAP_FACE",FACE,{"disambiguationData":[OSD([sQuery(id+"F0.wireOp",EDGE,"E0"),sQuery(id+"F0.wireOp",EDGE,"E1"),sQuery(id+"F0.wireOp",EDGE,"E2"),sQuery(id+"F0.wireOp",EDGE,"E3"),sQuery(id+"F0.wireOp",EDGE,"E4"),sQuery(id+"F0.wireOp",EDGE,"E5"),sQuery(id+"F0.wireOp",EDGE,"E6"),sQuery(id+"F0.wireOp",EDGE,"E7"),sQuery(id+"F0.wireOp",EDGE,"E8"),sQuery(id+"F0.wireOp",EDGE,"E9"),sQuery(id+"F0.wireOp",EDGE,"E19.0"),sQuery(id+"F0.wireOp",EDGE,"E19.1"),sQuery(id+"F0.wireOp",EDGE,"E19.2"),sQuery(id+"F0.wireOp",EDGE,"E19.3"),sQuery(id+"F0.wireOp",EDGE,"E19.4"),sQuery(id+"F0.wireOp",EDGE,"E19.5"),sQuery(id+"F0.wireOp",EDGE,"E19.6"),sQuery(id+"F0.wireOp",EDGE,"E19.7"),sQuery(id+"F0.wireOp",EDGE,"E19.8"),sQuery(id+"F0.wireOp",EDGE,"E19.9"),sQuery(id+"F0.wireOp",EDGE,"E19.10"),sQuery(id+"F0.wireOp",EDGE,"E19.11"),sQuery(id+"F0.wireOp",EDGE,"E19.12"),sQuery(id+"F0.wireOp",EDGE,"E19.13"),sQuery(id+"F0.wireOp",EDGE,"E19.14"),sQuery(id+"F0.wireOp",EDGE,"E20.0"),sQuery(id+"F0.wireOp",EDGE,"E21.0"),sQuery(id+"F0.wireOp",EDGE,"E22.0"),sQuery(id+"F0.wireOp",EDGE,"E23.0"),sQuery(id+"F0.wireOp",EDGE,"E24.0"),sQuery(id+"F0.wireOp",EDGE,"E25.0"),sQuery(id+"F0.wireOp",EDGE,"E26.0"),sQuery(id+"F0.wireOp",EDGE,"E27.0"),sQuery(id+"F0.wireOp",EDGE,"E28.0"),sQuery(id+"F0.wireOp",EDGE,"E29.0"),sQuery(id+"F0.wireOp",EDGE,"E30.0"),sQuery(id+"F0.wireOp",EDGE,"E31.0"),sQuery(id+"F0.wireOp",EDGE,"E32.0"),sQuery(id+"F0.wireOp",EDGE,"E33.0"),sQuery(id+"F0.wireOp",EDGE,"E34.0")])],"isStart":false}),makeQuery(id+"F4.opRevolve","SWEPT_FACE",FACE,{"disambiguationData":[OSD([sQuery(id+"F3.wireOp",EDGE,"E37")])]})]});
            var Q10;
            Q10=makeQuery(id+"F21.opBoolean","INTERSECT",EDGE,{"derivedFrom":[makeQuery(id+"F2.opExtrude","CAP_FACE",FACE,{"disambiguationData":[OSD([sQuery(id+"F0.wireOp",EDGE,"E0"),sQuery(id+"F0.wireOp",EDGE,"E1"),sQuery(id+"F0.wireOp",EDGE,"E2"),sQuery(id+"F0.wireOp",EDGE,"E3"),sQuery(id+"F0.wireOp",EDGE,"E4"),sQuery(id+"F0.wireOp",EDGE,"E5"),sQuery(id+"F0.wireOp",EDGE,"E6"),sQuery(id+"F0.wireOp",EDGE,"E7"),sQuery(id+"F0.wireOp",EDGE,"E8"),sQuery(id+"F0.wireOp",EDGE,"E9"),sQuery(id+"F0.wireOp",EDGE,"E19.0"),sQuery(id+"F0.wireOp",EDGE,"E19.1"),sQuery(id+"F0.wireOp",EDGE,"E19.2"),sQuery(id+"F0.wireOp",EDGE,"E19.3"),sQuery(id+"F0.wireOp",EDGE,"E19.4"),sQuery(id+"F0.wireOp",EDGE,"E19.5"),sQuery(id+"F0.wireOp",EDGE,"E19.6"),sQuery(id+"F0.wireOp",EDGE,"E19.7"),sQuery(id+"F0.wireOp",EDGE,"E19.8"),sQuery(id+"F0.wireOp",EDGE,"E19.9"),sQuery(id+"F0.wireOp",EDGE,"E19.10"),sQuery(id+"F0.wireOp",EDGE,"E19.11"),sQuery(id+"F0.wireOp",EDGE,"E19.12"),sQuery(id+"F0.wireOp",EDGE,"E19.13"),sQuery(id+"F0.wireOp",EDGE,"E19.14"),sQuery(id+"F0.wireOp",EDGE,"E20.0"),sQuery(id+"F0.wireOp",EDGE,"E21.0"),sQuery(id+"F0.wireOp",EDGE,"E22.0"),sQuery(id+"F0.wireOp",EDGE,"E23.0"),sQuery(id+"F0.wireOp",EDGE,"E24.0"),sQuery(id+"F0.wireOp",EDGE,"E25.0"),sQuery(id+"F0.wireOp",EDGE,"E26.0"),sQuery(id+"F0.wireOp",EDGE,"E27.0"),sQuery(id+"F0.wireOp",EDGE,"E28.0"),sQuery(id+"F0.wireOp",EDGE,"E29.0"),sQuery(id+"F0.wireOp",EDGE,"E30.0"),sQuery(id+"F0.wireOp",EDGE,"E31.0"),sQuery(id+"F0.wireOp",EDGE,"E32.0"),sQuery(id+"F0.wireOp",EDGE,"E33.0"),sQuery(id+"F0.wireOp",EDGE,"E34.0")])],"isStart":false}),makeQuery(id+"F20.opRevolve","SWEPT_FACE",FACE,{"disambiguationData":[OSD([sQuery(id+"F19.wireOp",EDGE,"E60")])]})]});
            var Q11;
            Q11=makeQuery(id+"F21.opBoolean","INTERSECT",EDGE,{"derivedFrom":[makeQuery(id+"F2.opExtrude","CAP_FACE",FACE,{"disambiguationData":[OSD([sQuery(id+"F0.wireOp",EDGE,"E0"),sQuery(id+"F0.wireOp",EDGE,"E1"),sQuery(id+"F0.wireOp",EDGE,"E2"),sQuery(id+"F0.wireOp",EDGE,"E3"),sQuery(id+"F0.wireOp",EDGE,"E4"),sQuery(id+"F0.wireOp",EDGE,"E5"),sQuery(id+"F0.wireOp",EDGE,"E6"),sQuery(id+"F0.wireOp",EDGE,"E7"),sQuery(id+"F0.wireOp",EDGE,"E8"),sQuery(id+"F0.wireOp",EDGE,"E9"),sQuery(id+"F0.wireOp",EDGE,"E19.0"),sQuery(id+"F0.wireOp",EDGE,"E19.1"),sQuery(id+"F0.wireOp",EDGE,"E19.2"),sQuery(id+"F0.wireOp",EDGE,"E19.3"),sQuery(id+"F0.wireOp",EDGE,"E19.4"),sQuery(id+"F0.wireOp",EDGE,"E19.5"),sQuery(id+"F0.wireOp",EDGE,"E19.6"),sQuery(id+"F0.wireOp",EDGE,"E19.7"),sQuery(id+"F0.wireOp",EDGE,"E19.8"),sQuery(id+"F0.wireOp",EDGE,"E19.9"),sQuery(id+"F0.wireOp",EDGE,"E19.10"),sQuery(id+"F0.wireOp",EDGE,"E19.11"),sQuery(id+"F0.wireOp",EDGE,"E19.12"),sQuery(id+"F0.wireOp",EDGE,"E19.13"),sQuery(id+"F0.wireOp",EDGE,"E19.14"),sQuery(id+"F0.wireOp",EDGE,"E20.0"),sQuery(id+"F0.wireOp",EDGE,"E21.0"),sQuery(id+"F0.wireOp",EDGE,"E22.0"),sQuery(id+"F0.wireOp",EDGE,"E23.0"),sQuery(id+"F0.wireOp",EDGE,"E24.0"),sQuery(id+"F0.wireOp",EDGE,"E25.0"),sQuery(id+"F0.wireOp",EDGE,"E26.0"),sQuery(id+"F0.wireOp",EDGE,"E27.0"),sQuery(id+"F0.wireOp",EDGE,"E28.0"),sQuery(id+"F0.wireOp",EDGE,"E29.0"),sQuery(id+"F0.wireOp",EDGE,"E30.0"),sQuery(id+"F0.wireOp",EDGE,"E31.0"),sQuery(id+"F0.wireOp",EDGE,"E32.0"),sQuery(id+"F0.wireOp",EDGE,"E33.0"),sQuery(id+"F0.wireOp",EDGE,"E34.0")])],"isStart":false}),makeQuery(id+"F17.opRevolve","SWEPT_FACE",FACE,{"disambiguationData":[OSD([sQuery(id+"F5.wireOp",EDGE,"E40")])]})]});
            var Q12;
            Q12=makeQuery(id+"F21.opBoolean","INTERSECT",EDGE,{"derivedFrom":[makeQuery(id+"F2.opExtrude","CAP_FACE",FACE,{"disambiguationData":[OSD([sQuery(id+"F0.wireOp",EDGE,"E0"),sQuery(id+"F0.wireOp",EDGE,"E1"),sQuery(id+"F0.wireOp",EDGE,"E2"),sQuery(id+"F0.wireOp",EDGE,"E3"),sQuery(id+"F0.wireOp",EDGE,"E4"),sQuery(id+"F0.wireOp",EDGE,"E5"),sQuery(id+"F0.wireOp",EDGE,"E6"),sQuery(id+"F0.wireOp",EDGE,"E7"),sQuery(id+"F0.wireOp",EDGE,"E8"),sQuery(id+"F0.wireOp",EDGE,"E9"),sQuery(id+"F0.wireOp",EDGE,"E19.0"),sQuery(id+"F0.wireOp",EDGE,"E19.1"),sQuery(id+"F0.wireOp",EDGE,"E19.2"),sQuery(id+"F0.wireOp",EDGE,"E19.3"),sQuery(id+"F0.wireOp",EDGE,"E19.4"),sQuery(id+"F0.wireOp",EDGE,"E19.5"),sQuery(id+"F0.wireOp",EDGE,"E19.6"),sQuery(id+"F0.wireOp",EDGE,"E19.7"),sQuery(id+"F0.wireOp",EDGE,"E19.8"),sQuery(id+"F0.wireOp",EDGE,"E19.9"),sQuery(id+"F0.wireOp",EDGE,"E19.10"),sQuery(id+"F0.wireOp",EDGE,"E19.11"),sQuery(id+"F0.wireOp",EDGE,"E19.12"),sQuery(id+"F0.wireOp",EDGE,"E19.13"),sQuery(id+"F0.wireOp",EDGE,"E19.14"),sQuery(id+"F0.wireOp",EDGE,"E20.0"),sQuery(id+"F0.wireOp",EDGE,"E21.0"),sQuery(id+"F0.wireOp",EDGE,"E22.0"),sQuery(id+"F0.wireOp",EDGE,"E23.0"),sQuery(id+"F0.wireOp",EDGE,"E24.0"),sQuery(id+"F0.wireOp",EDGE,"E25.0"),sQuery(id+"F0.wireOp",EDGE,"E26.0"),sQuery(id+"F0.wireOp",EDGE,"E27.0"),sQuery(id+"F0.wireOp",EDGE,"E28.0"),sQuery(id+"F0.wireOp",EDGE,"E29.0"),sQuery(id+"F0.wireOp",EDGE,"E30.0"),sQuery(id+"F0.wireOp",EDGE,"E31.0"),sQuery(id+"F0.wireOp",EDGE,"E32.0"),sQuery(id+"F0.wireOp",EDGE,"E33.0"),sQuery(id+"F0.wireOp",EDGE,"E34.0")])],"isStart":false}),makeQuery(id+"F9.opRevolve","SWEPT_FACE",FACE,{"disambiguationData":[OSD([sQuery(id+"F8.wireOp",EDGE,"E45")])]})]});
            var Q13;
            Q13=makeQuery(id+"F21.opBoolean","INTERSECT",EDGE,{"derivedFrom":[makeQuery(id+"F2.opExtrude","CAP_FACE",FACE,{"disambiguationData":[OSD([sQuery(id+"F0.wireOp",EDGE,"E0"),sQuery(id+"F0.wireOp",EDGE,"E1"),sQuery(id+"F0.wireOp",EDGE,"E2"),sQuery(id+"F0.wireOp",EDGE,"E3"),sQuery(id+"F0.wireOp",EDGE,"E4"),sQuery(id+"F0.wireOp",EDGE,"E5"),sQuery(id+"F0.wireOp",EDGE,"E6"),sQuery(id+"F0.wireOp",EDGE,"E7"),sQuery(id+"F0.wireOp",EDGE,"E8"),sQuery(id+"F0.wireOp",EDGE,"E9"),sQuery(id+"F0.wireOp",EDGE,"E19.0"),sQuery(id+"F0.wireOp",EDGE,"E19.1"),sQuery(id+"F0.wireOp",EDGE,"E19.2"),sQuery(id+"F0.wireOp",EDGE,"E19.3"),sQuery(id+"F0.wireOp",EDGE,"E19.4"),sQuery(id+"F0.wireOp",EDGE,"E19.5"),sQuery(id+"F0.wireOp",EDGE,"E19.6"),sQuery(id+"F0.wireOp",EDGE,"E19.7"),sQuery(id+"F0.wireOp",EDGE,"E19.8"),sQuery(id+"F0.wireOp",EDGE,"E19.9"),sQuery(id+"F0.wireOp",EDGE,"E19.10"),sQuery(id+"F0.wireOp",EDGE,"E19.11"),sQuery(id+"F0.wireOp",EDGE,"E19.12"),sQuery(id+"F0.wireOp",EDGE,"E19.13"),sQuery(id+"F0.wireOp",EDGE,"E19.14"),sQuery(id+"F0.wireOp",EDGE,"E20.0"),sQuery(id+"F0.wireOp",EDGE,"E21.0"),sQuery(id+"F0.wireOp",EDGE,"E22.0"),sQuery(id+"F0.wireOp",EDGE,"E23.0"),sQuery(id+"F0.wireOp",EDGE,"E24.0"),sQuery(id+"F0.wireOp",EDGE,"E25.0"),sQuery(id+"F0.wireOp",EDGE,"E26.0"),sQuery(id+"F0.wireOp",EDGE,"E27.0"),sQuery(id+"F0.wireOp",EDGE,"E28.0"),sQuery(id+"F0.wireOp",EDGE,"E29.0"),sQuery(id+"F0.wireOp",EDGE,"E30.0"),sQuery(id+"F0.wireOp",EDGE,"E31.0"),sQuery(id+"F0.wireOp",EDGE,"E32.0"),sQuery(id+"F0.wireOp",EDGE,"E33.0"),sQuery(id+"F0.wireOp",EDGE,"E34.0")])],"isStart":false}),makeQuery(id+"F7.opRevolve","SWEPT_FACE",FACE,{"disambiguationData":[OSD([sQuery(id+"F6.wireOp",EDGE,"E42")])]})]});
            var Q14;
            Q14=makeQuery(id+"F21.opBoolean","INTERSECT",EDGE,{"derivedFrom":[makeQuery(id+"F2.opExtrude","CAP_FACE",FACE,{"disambiguationData":[OSD([sQuery(id+"F0.wireOp",EDGE,"E0"),sQuery(id+"F0.wireOp",EDGE,"E1"),sQuery(id+"F0.wireOp",EDGE,"E2"),sQuery(id+"F0.wireOp",EDGE,"E3"),sQuery(id+"F0.wireOp",EDGE,"E4"),sQuery(id+"F0.wireOp",EDGE,"E5"),sQuery(id+"F0.wireOp",EDGE,"E6"),sQuery(id+"F0.wireOp",EDGE,"E7"),sQuery(id+"F0.wireOp",EDGE,"E8"),sQuery(id+"F0.wireOp",EDGE,"E9"),sQuery(id+"F0.wireOp",EDGE,"E19.0"),sQuery(id+"F0.wireOp",EDGE,"E19.1"),sQuery(id+"F0.wireOp",EDGE,"E19.2"),sQuery(id+"F0.wireOp",EDGE,"E19.3"),sQuery(id+"F0.wireOp",EDGE,"E19.4"),sQuery(id+"F0.wireOp",EDGE,"E19.5"),sQuery(id+"F0.wireOp",EDGE,"E19.6"),sQuery(id+"F0.wireOp",EDGE,"E19.7"),sQuery(id+"F0.wireOp",EDGE,"E19.8"),sQuery(id+"F0.wireOp",EDGE,"E19.9"),sQuery(id+"F0.wireOp",EDGE,"E19.10"),sQuery(id+"F0.wireOp",EDGE,"E19.11"),sQuery(id+"F0.wireOp",EDGE,"E19.12"),sQuery(id+"F0.wireOp",EDGE,"E19.13"),sQuery(id+"F0.wireOp",EDGE,"E19.14"),sQuery(id+"F0.wireOp",EDGE,"E20.0"),sQuery(id+"F0.wireOp",EDGE,"E21.0"),sQuery(id+"F0.wireOp",EDGE,"E22.0"),sQuery(id+"F0.wireOp",EDGE,"E23.0"),sQuery(id+"F0.wireOp",EDGE,"E24.0"),sQuery(id+"F0.wireOp",EDGE,"E25.0"),sQuery(id+"F0.wireOp",EDGE,"E26.0"),sQuery(id+"F0.wireOp",EDGE,"E27.0"),sQuery(id+"F0.wireOp",EDGE,"E28.0"),sQuery(id+"F0.wireOp",EDGE,"E29.0"),sQuery(id+"F0.wireOp",EDGE,"E30.0"),sQuery(id+"F0.wireOp",EDGE,"E31.0"),sQuery(id+"F0.wireOp",EDGE,"E32.0"),sQuery(id+"F0.wireOp",EDGE,"E33.0"),sQuery(id+"F0.wireOp",EDGE,"E34.0")])],"isStart":false}),makeQuery(id+"F11.opRevolve","SWEPT_FACE",FACE,{"disambiguationData":[OSD([sQuery(id+"F10.wireOp",EDGE,"E48")])]})]});
            var Q15;
            Q15=makeQuery(id+"F21.opBoolean","INTERSECT",EDGE,{"derivedFrom":[makeQuery(id+"F2.opExtrude","CAP_FACE",FACE,{"disambiguationData":[OSD([sQuery(id+"F0.wireOp",EDGE,"E0"),sQuery(id+"F0.wireOp",EDGE,"E1"),sQuery(id+"F0.wireOp",EDGE,"E2"),sQuery(id+"F0.wireOp",EDGE,"E3"),sQuery(id+"F0.wireOp",EDGE,"E4"),sQuery(id+"F0.wireOp",EDGE,"E5"),sQuery(id+"F0.wireOp",EDGE,"E6"),sQuery(id+"F0.wireOp",EDGE,"E7"),sQuery(id+"F0.wireOp",EDGE,"E8"),sQuery(id+"F0.wireOp",EDGE,"E9"),sQuery(id+"F0.wireOp",EDGE,"E19.0"),sQuery(id+"F0.wireOp",EDGE,"E19.1"),sQuery(id+"F0.wireOp",EDGE,"E19.2"),sQuery(id+"F0.wireOp",EDGE,"E19.3"),sQuery(id+"F0.wireOp",EDGE,"E19.4"),sQuery(id+"F0.wireOp",EDGE,"E19.5"),sQuery(id+"F0.wireOp",EDGE,"E19.6"),sQuery(id+"F0.wireOp",EDGE,"E19.7"),sQuery(id+"F0.wireOp",EDGE,"E19.8"),sQuery(id+"F0.wireOp",EDGE,"E19.9"),sQuery(id+"F0.wireOp",EDGE,"E19.10"),sQuery(id+"F0.wireOp",EDGE,"E19.11"),sQuery(id+"F0.wireOp",EDGE,"E19.12"),sQuery(id+"F0.wireOp",EDGE,"E19.13"),sQuery(id+"F0.wireOp",EDGE,"E19.14"),sQuery(id+"F0.wireOp",EDGE,"E20.0"),sQuery(id+"F0.wireOp",EDGE,"E21.0"),sQuery(id+"F0.wireOp",EDGE,"E22.0"),sQuery(id+"F0.wireOp",EDGE,"E23.0"),sQuery(id+"F0.wireOp",EDGE,"E24.0"),sQuery(id+"F0.wireOp",EDGE,"E25.0"),sQuery(id+"F0.wireOp",EDGE,"E26.0"),sQuery(id+"F0.wireOp",EDGE,"E27.0"),sQuery(id+"F0.wireOp",EDGE,"E28.0"),sQuery(id+"F0.wireOp",EDGE,"E29.0"),sQuery(id+"F0.wireOp",EDGE,"E30.0"),sQuery(id+"F0.wireOp",EDGE,"E31.0"),sQuery(id+"F0.wireOp",EDGE,"E32.0"),sQuery(id+"F0.wireOp",EDGE,"E33.0"),sQuery(id+"F0.wireOp",EDGE,"E34.0")])],"isStart":false}),makeQuery(id+"F13.opRevolve","SWEPT_FACE",FACE,{"disambiguationData":[OSD([sQuery(id+"F12.wireOp",EDGE,"E51")])]})]});
            var Q16;
            Q16=makeQuery(id+"F21.opBoolean","INTERSECT",EDGE,{"derivedFrom":[makeQuery(id+"F2.opExtrude","CAP_FACE",FACE,{"disambiguationData":[OSD([sQuery(id+"F0.wireOp",EDGE,"E0"),sQuery(id+"F0.wireOp",EDGE,"E1"),sQuery(id+"F0.wireOp",EDGE,"E2"),sQuery(id+"F0.wireOp",EDGE,"E3"),sQuery(id+"F0.wireOp",EDGE,"E4"),sQuery(id+"F0.wireOp",EDGE,"E5"),sQuery(id+"F0.wireOp",EDGE,"E6"),sQuery(id+"F0.wireOp",EDGE,"E7"),sQuery(id+"F0.wireOp",EDGE,"E8"),sQuery(id+"F0.wireOp",EDGE,"E9"),sQuery(id+"F0.wireOp",EDGE,"E19.0"),sQuery(id+"F0.wireOp",EDGE,"E19.1"),sQuery(id+"F0.wireOp",EDGE,"E19.2"),sQuery(id+"F0.wireOp",EDGE,"E19.3"),sQuery(id+"F0.wireOp",EDGE,"E19.4"),sQuery(id+"F0.wireOp",EDGE,"E19.5"),sQuery(id+"F0.wireOp",EDGE,"E19.6"),sQuery(id+"F0.wireOp",EDGE,"E19.7"),sQuery(id+"F0.wireOp",EDGE,"E19.8"),sQuery(id+"F0.wireOp",EDGE,"E19.9"),sQuery(id+"F0.wireOp",EDGE,"E19.10"),sQuery(id+"F0.wireOp",EDGE,"E19.11"),sQuery(id+"F0.wireOp",EDGE,"E19.12"),sQuery(id+"F0.wireOp",EDGE,"E19.13"),sQuery(id+"F0.wireOp",EDGE,"E19.14"),sQuery(id+"F0.wireOp",EDGE,"E20.0"),sQuery(id+"F0.wireOp",EDGE,"E21.0"),sQuery(id+"F0.wireOp",EDGE,"E22.0"),sQuery(id+"F0.wireOp",EDGE,"E23.0"),sQuery(id+"F0.wireOp",EDGE,"E24.0"),sQuery(id+"F0.wireOp",EDGE,"E25.0"),sQuery(id+"F0.wireOp",EDGE,"E26.0"),sQuery(id+"F0.wireOp",EDGE,"E27.0"),sQuery(id+"F0.wireOp",EDGE,"E28.0"),sQuery(id+"F0.wireOp",EDGE,"E29.0"),sQuery(id+"F0.wireOp",EDGE,"E30.0"),sQuery(id+"F0.wireOp",EDGE,"E31.0"),sQuery(id+"F0.wireOp",EDGE,"E32.0"),sQuery(id+"F0.wireOp",EDGE,"E33.0"),sQuery(id+"F0.wireOp",EDGE,"E34.0")])],"isStart":false}),makeQuery(id+"F18.opRevolve","SWEPT_FACE",FACE,{"disambiguationData":[OSD([sQuery(id+"F16.wireOp",EDGE,"E57")])]})]});
            var Q17;
            Q17=makeQuery(id+"F21.opBoolean","INTERSECT",EDGE,{"derivedFrom":[makeQuery(id+"F2.opExtrude","CAP_FACE",FACE,{"disambiguationData":[OSD([sQuery(id+"F0.wireOp",EDGE,"E0"),sQuery(id+"F0.wireOp",EDGE,"E1"),sQuery(id+"F0.wireOp",EDGE,"E2"),sQuery(id+"F0.wireOp",EDGE,"E3"),sQuery(id+"F0.wireOp",EDGE,"E4"),sQuery(id+"F0.wireOp",EDGE,"E5"),sQuery(id+"F0.wireOp",EDGE,"E6"),sQuery(id+"F0.wireOp",EDGE,"E7"),sQuery(id+"F0.wireOp",EDGE,"E8"),sQuery(id+"F0.wireOp",EDGE,"E9"),sQuery(id+"F0.wireOp",EDGE,"E19.0"),sQuery(id+"F0.wireOp",EDGE,"E19.1"),sQuery(id+"F0.wireOp",EDGE,"E19.2"),sQuery(id+"F0.wireOp",EDGE,"E19.3"),sQuery(id+"F0.wireOp",EDGE,"E19.4"),sQuery(id+"F0.wireOp",EDGE,"E19.5"),sQuery(id+"F0.wireOp",EDGE,"E19.6"),sQuery(id+"F0.wireOp",EDGE,"E19.7"),sQuery(id+"F0.wireOp",EDGE,"E19.8"),sQuery(id+"F0.wireOp",EDGE,"E19.9"),sQuery(id+"F0.wireOp",EDGE,"E19.10"),sQuery(id+"F0.wireOp",EDGE,"E19.11"),sQuery(id+"F0.wireOp",EDGE,"E19.12"),sQuery(id+"F0.wireOp",EDGE,"E19.13"),sQuery(id+"F0.wireOp",EDGE,"E19.14"),sQuery(id+"F0.wireOp",EDGE,"E20.0"),sQuery(id+"F0.wireOp",EDGE,"E21.0"),sQuery(id+"F0.wireOp",EDGE,"E22.0"),sQuery(id+"F0.wireOp",EDGE,"E23.0"),sQuery(id+"F0.wireOp",EDGE,"E24.0"),sQuery(id+"F0.wireOp",EDGE,"E25.0"),sQuery(id+"F0.wireOp",EDGE,"E26.0"),sQuery(id+"F0.wireOp",EDGE,"E27.0"),sQuery(id+"F0.wireOp",EDGE,"E28.0"),sQuery(id+"F0.wireOp",EDGE,"E29.0"),sQuery(id+"F0.wireOp",EDGE,"E30.0"),sQuery(id+"F0.wireOp",EDGE,"E31.0"),sQuery(id+"F0.wireOp",EDGE,"E32.0"),sQuery(id+"F0.wireOp",EDGE,"E33.0"),sQuery(id+"F0.wireOp",EDGE,"E34.0")])],"isStart":false}),makeQuery(id+"F15.opRevolve","SWEPT_FACE",FACE,{"disambiguationData":[OSD([sQuery(id+"F14.wireOp",EDGE,"E54")])]})]});
            fillet(context, id + "F26", {"entities" : qUnion([Q0, Q1, Q2, Q3, Q4, Q5, Q6, Q7, Q8, Q9, Q10, Q11, Q12, Q13, Q14, Q15, Q16, Q17]), "radius" : 1.32 * mm, "tangentPropagation" : true, "allowEdgeOverflow" : false});
        }
    });
